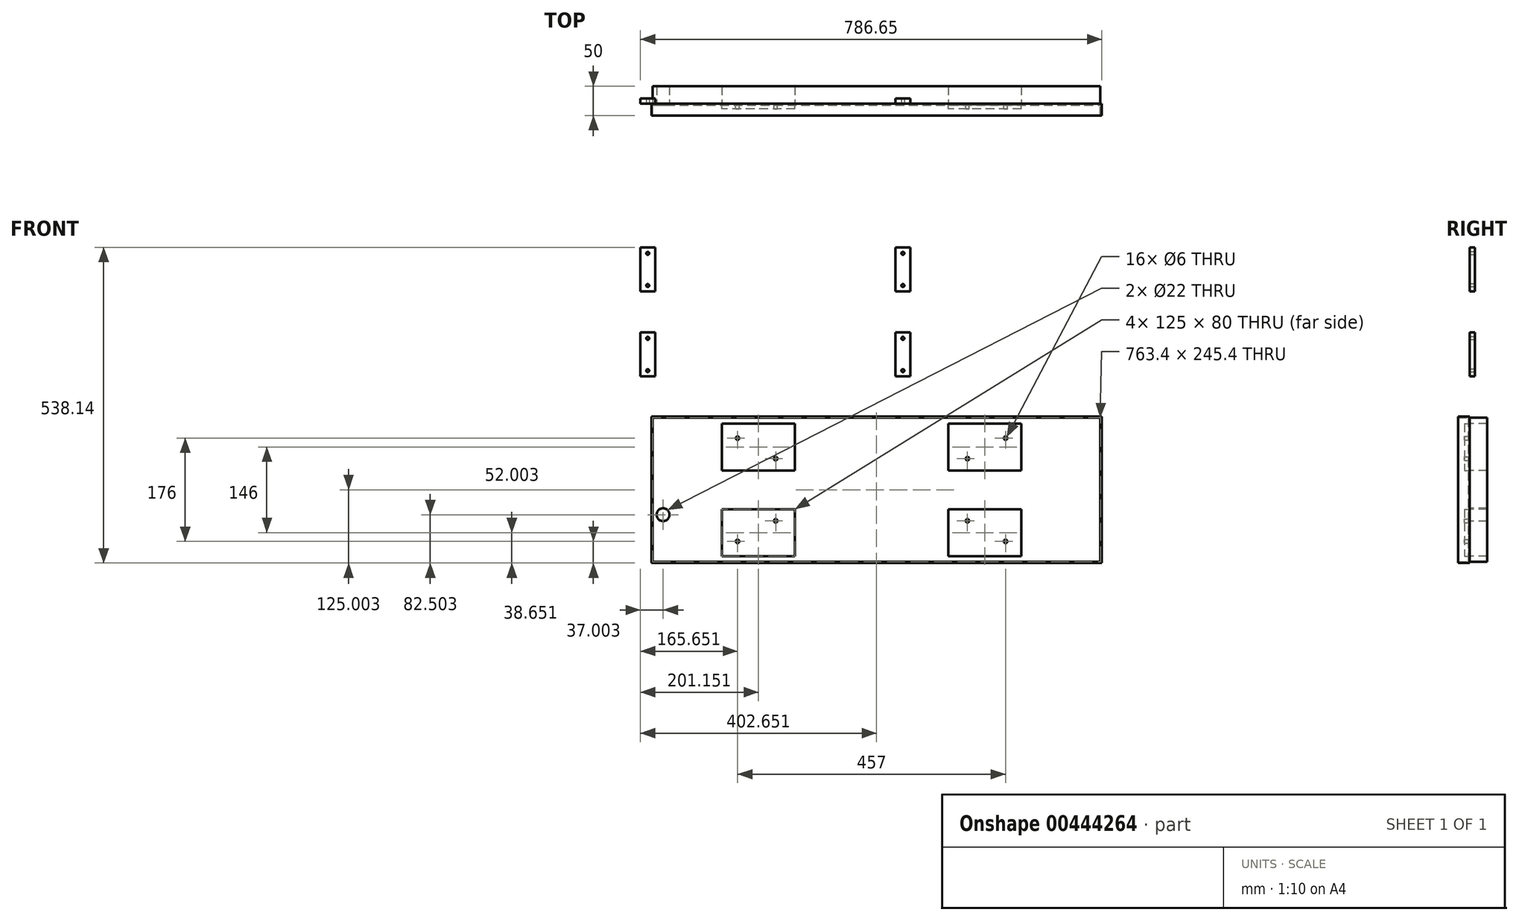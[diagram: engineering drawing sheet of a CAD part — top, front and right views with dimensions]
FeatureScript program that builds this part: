
annotation { "Feature Type Name" : "Feature", "Feature Type Description" : "" }
export const myFeature = defineFeature(function(context is Context, id is Id, definition is map)
    precondition{}
    {
        {
            var Q0;
            Q0=qCreatedBy(makeId("Front.planeOp"),FACE);
            var sketch = newSketch(context, id + "F0", { "sketchPlane" : qUnion([Q0])});
            skLineSegment(sketch, "E0", {"start": v(-733.37, -560) * mm, "end": v(-733.37, 560) * mm});
            skLineSegment(sketch, "E1", {"start": v(-733.37, -560) * mm, "end": v(876.63, -560) * mm});
            skLineSegment(sketch, "E2", {"start": v(-733.37, 560) * mm, "end": v(876.63, 560) * mm});
            skLineSegment(sketch, "E3", {"start": v(876.63, -560) * mm, "end": v(876.63, 560) * mm});
            skLineSegment(sketch, "E4", {"start": v(336.63, -506) * mm, "end": v(336.63, -560) * mm});
            skLineSegment(sketch, "E5", {"start": v(336.63, -506) * mm, "end": v(876.63, -506) * mm});
            skLineSegment(sketch, "E6", {"start": v(526.63, -552) * mm, "end": v(640.63, -552) * mm});
            skLineSegment(sketch, "E7", {"start": v(526.63, -533.38) * mm, "end": v(640.63, -533.38) * mm});
            skLineSegment(sketch, "E8", {"start": v(336.63, -544) * mm, "end": v(526.63, -544) * mm});
            skLineSegment(sketch, "E9", {"start": v(526.63, -506) * mm, "end": v(526.63, -560) * mm});
            skLineSegment(sketch, "E10", {"start": v(604.63, -533.38) * mm, "end": v(604.63, -560) * mm});
            skLineSegment(sketch, "E11", {"start": v(640.63, -542) * mm, "end": v(876.63, -542) * mm});
            skLineSegment(sketch, "E12", {"start": v(730.63, -524) * mm, "end": v(876.63, -524) * mm});
            skLineSegment(sketch, "E13", {"start": v(640.63, -516) * mm, "end": v(730.63, -516) * mm});
            skLineSegment(sketch, "E14", {"start": v(726.24, -520.82) * mm, "end": v(711.38, -538.9) * mm});
            skLineSegment(sketch, "E15", {"start": v(640.63, -506) * mm, "end": v(640.63, -560) * mm});
            skLineSegment(sketch, "E16", {"start": v(674.63, -506) * mm, "end": v(674.63, -542) * mm});
            skLineSegment(sketch, "E17", {"start": v(642.51, -529.04) * mm, "end": v(657.96, -529.04) * mm});
            skCircle(sketch, "E18", {"center": v(650.23, -529.04) * mm, "radius": 5.94 * mm});
            skCircle(sketch, "E19", {"center": v(650.23, -529.04) * mm, "radius": 2.93 * mm});
            skLineSegment(sketch, "E20", {"start": v(650.23, -521.32) * mm, "end": v(650.23, -536.77) * mm});
            skLineSegment(sketch, "E21", {"start": v(670.15, -523.1) * mm, "end": v(670.15, -534.99) * mm});
            skLineSegment(sketch, "E22", {"start": v(661.98, -526.11) * mm, "end": v(661.98, -531.98) * mm});
            skLineSegment(sketch, "E23", {"start": v(670.15, -534.99) * mm, "end": v(661.98, -531.98) * mm});
            skLineSegment(sketch, "E24", {"start": v(660.33, -529.04) * mm, "end": v(672, -529.04) * mm});
            skLineSegment(sketch, "E25", {"start": v(670.15, -523.1) * mm, "end": v(661.98, -526.11) * mm});
            skLineSegment(sketch, "E26", {"start": v(708.63, -506) * mm, "end": v(708.63, -542) * mm});
            skLineSegment(sketch, "E27", {"start": v(730.63, -506) * mm, "end": v(730.63, -542) * mm});
            skLineSegment(sketch, "E28", {"start": v(820.63, -542) * mm, "end": v(820.63, -560) * mm});
            skLineSegment(sketch, "E29", {"start": v(820.63, -506) * mm, "end": v(820.63, -524) * mm});
            skLineSegment(sketch, "E30", {"start": v(876.63, 548) * mm, "end": v(680.63, 548) * mm});
            skLineSegment(sketch, "E31", {"start": v(876.63, 536) * mm, "end": v(680.63, 536) * mm});
            skLineSegment(sketch, "E32", {"start": v(876.63, 524) * mm, "end": v(680.63, 524) * mm});
            skLineSegment(sketch, "E33", {"start": v(708.63, 560) * mm, "end": v(708.63, 524) * mm});
            skLineSegment(sketch, "E34", {"start": v(680.63, 560) * mm, "end": v(680.63, 524) * mm});
            skLineSegment(sketch, "E35", {"start": v(689.47, 550.2) * mm, "end": v(699.07, 550.2) * mm});
            skLineSegment(sketch, "E36", {"start": v(826.63, 560) * mm, "end": v(826.63, 524) * mm});
            skLineSegment(sketch, "E37", {"start": v(856.63, 560) * mm, "end": v(856.63, 524) * mm});
            skLineSegment(sketch, "E38", {"start": v(689.47, 550.2) * mm, "end": v(694.27, 558.2) * mm});
            skLineSegment(sketch, "E39", {"start": v(694.27, 558.2) * mm, "end": v(699.07, 550.2) * mm});
            skLineSegment(sketch, "E40", {"start": v(689.47, 538.2) * mm, "end": v(699.07, 538.2) * mm});
            skLineSegment(sketch, "E41", {"start": v(689.47, 538.2) * mm, "end": v(694.27, 546.2) * mm});
            skLineSegment(sketch, "E42", {"start": v(694.27, 546.2) * mm, "end": v(699.07, 538.2) * mm});
            skLineSegment(sketch, "E43", {"start": v(1010.4, -269.61) * mm, "end": v(1030.4, -269.61) * mm});
            skLineSegment(sketch, "E44", {"start": v(1030.4, -269.61) * mm, "end": v(1030.4, -249.61) * mm});
            skLineSegment(sketch, "E45", {"start": v(1030.4, -249.61) * mm, "end": v(1010.4, -269.61) * mm});
            skLineSegment(sketch, "E46", {"start": v(1013.65, 191.18) * mm, "end": v(1016.53, 186.18) * mm});
            skLineSegment(sketch, "E47", {"start": v(1016.53, 186.18) * mm, "end": v(1022.88, 197.18) * mm});
            skLineSegment(sketch, "E48", {"start": v(1022.88, 197.18) * mm, "end": v(1035.58, 197.18) * mm});
            skLineSegment(sketch, "E49", {"start": v(1013.65, 191.18) * mm, "end": v(1019.42, 191.18) * mm});
            skLineSegment(sketch, "E50", {"start": v(1039.7, 191.18) * mm, "end": v(1042.58, 186.18) * mm});
            skLineSegment(sketch, "E51", {"start": v(1042.58, 186.18) * mm, "end": v(1048.93, 197.18) * mm});
            skCircle(sketch, "E52", {"center": v(1042.58, 189.5) * mm, "radius": 1.67 * mm});
            skArc(sketch, "E53", {"start": v(1013.3, 197.53) * mm, "mid": v(1011.2, 191.68) * mm, "end": v(1013.3, 185.83) * mm});
            skArc(sketch, "E54", {"start": v(1053, 185.83) * mm, "mid": v(1055.1, 191.68) * mm, "end": v(1053, 197.53) * mm});
            skLineSegment(sketch, "E55", {"start": v(1036.28, 210.45) * mm, "end": v(1039.16, 205.45) * mm});
            skLineSegment(sketch, "E56", {"start": v(1039.16, 205.45) * mm, "end": v(1045.51, 216.45) * mm});
            skLineSegment(sketch, "E57", {"start": v(1045.51, 216.45) * mm, "end": v(1059.96, 216.45) * mm});
            skLineSegment(sketch, "E58", {"start": v(1036.28, 210.45) * mm, "end": v(1042.05, 210.45) * mm});
            skCircle(sketch, "E59", {"center": v(1045.51, 216.45) * mm, "radius": 1.57 * mm});
            skLineSegment(sketch, "E60", {"start": v(1032.26, 205.45) * mm, "end": v(1062.26, 205.45) * mm});
            skLineSegment(sketch, "E61", {"start": v(996.15, 134.22) * mm, "end": v(999.04, 129.22) * mm});
            skLineSegment(sketch, "E62", {"start": v(999.04, 129.22) * mm, "end": v(1005.4, 140.22) * mm});
            skLineSegment(sketch, "E63", {"start": v(1005.4, 140.22) * mm, "end": v(1019.84, 140.22) * mm});
            skLineSegment(sketch, "E64", {"start": v(996.15, 134.22) * mm, "end": v(1001.93, 134.22) * mm});
            skLineSegment(sketch, "E65", {"start": v(996.15, 114.48) * mm, "end": v(999.04, 109.48) * mm});
            skLineSegment(sketch, "E66", {"start": v(999.04, 109.48) * mm, "end": v(1005.4, 120.48) * mm});
            skLineSegment(sketch, "E67", {"start": v(1005.4, 120.48) * mm, "end": v(1019.84, 120.48) * mm});
            skLineSegment(sketch, "E68", {"start": v(996.15, 114.48) * mm, "end": v(1001.93, 114.48) * mm});
            skLineSegment(sketch, "E69", {"start": v(995.98, 95.05) * mm, "end": v(998.86, 90.05) * mm});
            skLineSegment(sketch, "E70", {"start": v(998.86, 90.05) * mm, "end": v(1005.21, 101.05) * mm});
            skLineSegment(sketch, "E71", {"start": v(1005.21, 101.05) * mm, "end": v(1017.9, 101.05) * mm});
            skLineSegment(sketch, "E72", {"start": v(995.98, 95.05) * mm, "end": v(1001.75, 95.05) * mm});
            skLineSegment(sketch, "E73", {"start": v(996.27, 77.08) * mm, "end": v(999.16, 72.08) * mm});
            skLineSegment(sketch, "E74", {"start": v(999.16, 72.08) * mm, "end": v(1005.51, 83.08) * mm});
            skLineSegment(sketch, "E75", {"start": v(1005.51, 83.08) * mm, "end": v(1018.27, 83.08) * mm});
            skLineSegment(sketch, "E76", {"start": v(996.27, 77.08) * mm, "end": v(1002.05, 77.08) * mm});
            skLineSegment(sketch, "E77", {"start": v(996.27, 59.66) * mm, "end": v(999.16, 54.66) * mm});
            skLineSegment(sketch, "E78", {"start": v(999.16, 54.66) * mm, "end": v(1005.51, 65.66) * mm});
            skLineSegment(sketch, "E79", {"start": v(1005.51, 65.66) * mm, "end": v(1018.27, 65.66) * mm});
            skLineSegment(sketch, "E80", {"start": v(996.27, 59.66) * mm, "end": v(1002.05, 59.66) * mm});
            skLineSegment(sketch, "E81", {"start": v(998.2, 306.77) * mm, "end": v(1001.09, 301.77) * mm});
            skLineSegment(sketch, "E82", {"start": v(1001.09, 301.77) * mm, "end": v(1007.44, 312.77) * mm});
            skLineSegment(sketch, "E83", {"start": v(1007.44, 312.77) * mm, "end": v(1021.88, 312.77) * mm});
            skLineSegment(sketch, "E84", {"start": v(998.2, 306.77) * mm, "end": v(1003.97, 306.77) * mm});
            skLineSegment(sketch, "E85", {"start": v(994.19, 301.77) * mm, "end": v(1024.19, 301.77) * mm});
            skLineSegment(sketch, "E86", {"start": v(998.2, 287.03) * mm, "end": v(1001.09, 282.03) * mm});
            skLineSegment(sketch, "E87", {"start": v(1001.09, 282.03) * mm, "end": v(1007.44, 293.03) * mm});
            skLineSegment(sketch, "E88", {"start": v(1007.44, 293.03) * mm, "end": v(1021.88, 293.03) * mm});
            skLineSegment(sketch, "E89", {"start": v(998.2, 287.03) * mm, "end": v(1003.97, 287.03) * mm});
            skLineSegment(sketch, "E90", {"start": v(994.19, 282.03) * mm, "end": v(1024.19, 282.03) * mm});
            skLineSegment(sketch, "E91", {"start": v(998.02, 267.6) * mm, "end": v(1000.9, 262.6) * mm});
            skLineSegment(sketch, "E92", {"start": v(1000.9, 262.6) * mm, "end": v(1007.26, 273.6) * mm});
            skLineSegment(sketch, "E93", {"start": v(1007.26, 273.6) * mm, "end": v(1019.95, 273.6) * mm});
            skLineSegment(sketch, "E94", {"start": v(998.02, 267.6) * mm, "end": v(1003.8, 267.6) * mm});
            skLineSegment(sketch, "E95", {"start": v(994, 262.6) * mm, "end": v(1024, 262.6) * mm});
            skLineSegment(sketch, "E96", {"start": v(998.32, 249.64) * mm, "end": v(1001.2, 244.64) * mm});
            skLineSegment(sketch, "E97", {"start": v(1001.2, 244.64) * mm, "end": v(1007.56, 255.64) * mm});
            skLineSegment(sketch, "E98", {"start": v(1007.56, 255.64) * mm, "end": v(1020.32, 255.64) * mm});
            skLineSegment(sketch, "E99", {"start": v(998.32, 249.64) * mm, "end": v(1004.1, 249.64) * mm});
            skLineSegment(sketch, "E100", {"start": v(994.3, 244.64) * mm, "end": v(1024.3, 244.64) * mm});
            skLineSegment(sketch, "E101", {"start": v(998.32, 232.21) * mm, "end": v(1001.2, 227.21) * mm});
            skLineSegment(sketch, "E102", {"start": v(1001.2, 227.21) * mm, "end": v(1007.56, 238.21) * mm});
            skLineSegment(sketch, "E103", {"start": v(1007.56, 238.21) * mm, "end": v(1020.32, 238.21) * mm});
            skLineSegment(sketch, "E104", {"start": v(998.32, 232.21) * mm, "end": v(1004.1, 232.21) * mm});
            skLineSegment(sketch, "E105", {"start": v(994.19, 227.42) * mm, "end": v(1024.19, 227.42) * mm});
            skLineSegment(sketch, "E106", {"start": v(998.72, 191.18) * mm, "end": v(1001.6, 186.18) * mm});
            skLineSegment(sketch, "E107", {"start": v(1001.6, 186.18) * mm, "end": v(1007.96, 197.18) * mm});
            skLineSegment(sketch, "E108", {"start": v(999.54, 210.87) * mm, "end": v(1002.43, 205.87) * mm});
            skLineSegment(sketch, "E109", {"start": v(1002.43, 205.87) * mm, "end": v(1008.78, 216.87) * mm});
            skCircle(sketch, "E110", {"center": v(1002.43, 209.2) * mm, "radius": 0.83 * mm});
            skLineSegment(sketch, "E111", {"start": v(996.43, 205.87) * mm, "end": v(1010.43, 205.87) * mm});
            skLineSegment(sketch, "E112", {"start": v(1018.14, 210.45) * mm, "end": v(1021.03, 205.45) * mm});
            skLineSegment(sketch, "E113", {"start": v(1021.03, 205.45) * mm, "end": v(1027.38, 216.45) * mm});
            skLineSegment(sketch, "E114", {"start": v(1018.14, 210.45) * mm, "end": v(1023.91, 210.45) * mm});
            skLineSegment(sketch, "E115", {"start": v(1015.03, 205.45) * mm, "end": v(1029.03, 205.45) * mm});
            skLineSegment(sketch, "E116", {"start": v(997.04, 174.08) * mm, "end": v(999.93, 169.08) * mm});
            skLineSegment(sketch, "E117", {"start": v(999.93, 169.08) * mm, "end": v(1006.28, 180.08) * mm});
            skLineSegment(sketch, "E118", {"start": v(1007.93, 169.08) * mm, "end": v(993.93, 169.08) * mm});
            skLineSegment(sketch, "E119", {"start": v(1040.3, 232.21) * mm, "end": v(1043.18, 227.21) * mm});
            skLineSegment(sketch, "E120", {"start": v(1043.18, 227.21) * mm, "end": v(1049.53, 238.21) * mm});
            skLineSegment(sketch, "E121", {"start": v(1049.53, 238.21) * mm, "end": v(1062.29, 238.21) * mm});
            skLineSegment(sketch, "E122", {"start": v(1040.3, 232.21) * mm, "end": v(1046.06, 232.21) * mm});
            skLineSegment(sketch, "E123", {"start": v(1036.16, 227.42) * mm, "end": v(1066.16, 227.42) * mm});
            skLineSegment(sketch, "E124", {"start": v(1040.3, 57.02) * mm, "end": v(1043.18, 52.02) * mm});
            skLineSegment(sketch, "E125", {"start": v(1043.18, 52.02) * mm, "end": v(1049.53, 63.02) * mm});
            skLineSegment(sketch, "E126", {"start": v(1049.53, 63.02) * mm, "end": v(1062.29, 63.02) * mm});
            skLineSegment(sketch, "E127", {"start": v(1040.3, 57.02) * mm, "end": v(1046.06, 57.02) * mm});
            skLineSegment(sketch, "E128", {"start": v(1016.1, 37.9) * mm, "end": v(1018.98, 32.9) * mm});
            skLineSegment(sketch, "E129", {"start": v(1018.98, 32.9) * mm, "end": v(1025.33, 43.9) * mm});
            skLineSegment(sketch, "E130", {"start": v(1016.1, 37.9) * mm, "end": v(1021.87, 37.9) * mm});
            skLineSegment(sketch, "E131", {"start": v(997.5, 38.32) * mm, "end": v(1000.38, 33.32) * mm});
            skLineSegment(sketch, "E132", {"start": v(1000.38, 33.32) * mm, "end": v(1006.73, 44.32) * mm});
            skCircle(sketch, "E133", {"center": v(1000.38, 36.65) * mm, "radius": 0.83 * mm});
            skLineSegment(sketch, "E134", {"start": v(517.21, 1.91) * mm, "end": v(-241.59, 1.91) * mm});
            skArc(sketch, "E135", {"start": v(517.21, 1.91) * mm, "mid": v(520.46, 3.26) * mm, "end": v(521.81, 6.51) * mm});
            skLineSegment(sketch, "E136", {"start": v(521.81, 21.91) * mm, "end": v(519.51, 21.91) * mm});
            skLineSegment(sketch, "E137", {"start": v(521.81, 6.51) * mm, "end": v(521.81, 21.91) * mm});
            skLineSegment(sketch, "E138", {"start": v(519.51, 6.51) * mm, "end": v(519.51, 21.91) * mm});
            skArc(sketch, "E139", {"start": v(517.21, 4.21) * mm, "mid": v(518.84, 4.89) * mm, "end": v(519.51, 6.51) * mm});
            skLineSegment(sketch, "E140", {"start": v(-246.19, 21.91) * mm, "end": v(-243.89, 21.91) * mm});
            skLineSegment(sketch, "E141", {"start": v(-246.19, 6.51) * mm, "end": v(-246.19, 21.91) * mm});
            skLineSegment(sketch, "E142", {"start": v(-243.89, 6.51) * mm, "end": v(-243.89, 21.91) * mm});
            skArc(sketch, "E143", {"start": v(-246.19, 6.51) * mm, "mid": v(-244.84, 3.26) * mm, "end": v(-241.59, 1.91) * mm});
            skArc(sketch, "E144", {"start": v(-243.89, 6.51) * mm, "mid": v(-243.22, 4.89) * mm, "end": v(-241.59, 4.21) * mm});
            skLineSegment(sketch, "E145", {"start": v(517.21, 4.21) * mm, "end": v(-241.59, 4.21) * mm});
            skLineSegment(sketch, "E146", {"start": v(384.81, 13.21) * mm, "end": v(259.81, 13.21) * mm});
            skLineSegment(sketch, "E147", {"start": v(-246.19, 21.91) * mm, "end": v(521.81, 21.91) * mm});
            skLineSegment(sketch, "E148", {"start": v(-62.19, -7.09) * mm, "end": v(-87.19, -7.09) * mm});
            skLineSegment(sketch, "E149", {"start": v(-87.19, 1.91) * mm, "end": v(-87.19, -7.09) * mm});
            skLineSegment(sketch, "E150", {"start": v(-62.19, 1.91) * mm, "end": v(-62.19, -7.09) * mm});
            skLineSegment(sketch, "E151", {"start": v(347.81, -7.09) * mm, "end": v(372.81, -7.09) * mm});
            skLineSegment(sketch, "E152", {"start": v(372.81, 1.91) * mm, "end": v(372.81, -7.09) * mm});
            skLineSegment(sketch, "E153", {"start": v(347.81, 1.91) * mm, "end": v(347.81, -7.09) * mm});
            skLineSegment(sketch, "E154", {"start": v(-387.97, 4.21) * mm, "end": v(-628.77, 4.21) * mm});
            skLineSegment(sketch, "E155", {"start": v(-387.97, 1.91) * mm, "end": v(-628.77, 1.91) * mm});
            skLineSegment(sketch, "E156", {"start": v(-398.37, -7.09) * mm, "end": v(-454.87, -7.09) * mm});
            skArc(sketch, "E157", {"start": v(-387.97, 1.91) * mm, "mid": v(-384.72, 3.26) * mm, "end": v(-383.37, 6.51) * mm});
            skLineSegment(sketch, "E158", {"start": v(-383.37, 21.91) * mm, "end": v(-385.67, 21.91) * mm});
            skLineSegment(sketch, "E159", {"start": v(-383.37, 6.51) * mm, "end": v(-383.37, 21.91) * mm});
            skLineSegment(sketch, "E160", {"start": v(-385.67, 6.51) * mm, "end": v(-385.67, 21.91) * mm});
            skArc(sketch, "E161", {"start": v(-387.97, 4.21) * mm, "mid": v(-386.34, 4.89) * mm, "end": v(-385.67, 6.51) * mm});
            skLineSegment(sketch, "E162", {"start": v(-633.37, 6.51) * mm, "end": v(-633.37, 21.91) * mm});
            skLineSegment(sketch, "E163", {"start": v(-631.07, 6.51) * mm, "end": v(-631.07, 21.91) * mm});
            skArc(sketch, "E164", {"start": v(-633.37, 6.51) * mm, "mid": v(-632.02, 3.26) * mm, "end": v(-628.77, 1.91) * mm});
            skArc(sketch, "E165", {"start": v(-631.07, 6.51) * mm, "mid": v(-630.4, 4.89) * mm, "end": v(-628.77, 4.21) * mm});
            skLineSegment(sketch, "E166", {"start": v(-398.37, 1.91) * mm, "end": v(-398.37, -7.09) * mm});
            skLineSegment(sketch, "E167", {"start": v(-473.37, 1.91) * mm, "end": v(-473.37, -7.09) * mm});
            skLineSegment(sketch, "E168", {"start": v(-618.37, -7.09) * mm, "end": v(-543.37, -7.09) * mm});
            skLineSegment(sketch, "E169", {"start": v(-618.37, 1.91) * mm, "end": v(-618.37, -7.09) * mm});
            skLineSegment(sketch, "E170", {"start": v(-543.37, 1.91) * mm, "end": v(-543.37, -7.09) * mm});
            skLineSegment(sketch, "E171", {"start": v(-383.37, 21.91) * mm, "end": v(-633.37, 21.91) * mm});
            skLineSegment(sketch, "E172", {"start": v(-233.44, -8.09) * mm, "end": v(-233.75, 1.91) * mm});
            skLineSegment(sketch, "E173", {"start": v(-234.02, -18.09) * mm, "end": v(-218.36, -18.09) * mm});
            skLineSegment(sketch, "E174", {"start": v(-226.19, 1.91) * mm, "end": v(-226.19, -16.4) * mm});
            skLineSegment(sketch, "E175", {"start": v(-235.19, 4.21) * mm, "end": v(-235.19, 1.91) * mm});
            skLineSegment(sketch, "E176", {"start": v(-233.44, -18.09) * mm, "end": v(-233.44, -14.8) * mm});
            skLineSegment(sketch, "E177", {"start": v(-233.44, -8.09) * mm, "end": v(-233.44, -14.8) * mm});
            skLineSegment(sketch, "E178", {"start": v(-234.02, -18.09) * mm, "end": v(-234.52, -28.09) * mm});
            skLineSegment(sketch, "E179", {"start": v(-234.02, -8.09) * mm, "end": v(-218.36, -8.09) * mm});
            skLineSegment(sketch, "E180", {"start": v(-234.02, -8.09) * mm, "end": v(-233.44, -9.1) * mm});
            skLineSegment(sketch, "E181", {"start": v(-218.94, -18.09) * mm, "end": v(-218.94, -14.8) * mm});
            skLineSegment(sketch, "E182", {"start": v(-234.02, -18.09) * mm, "end": v(-233.44, -17.08) * mm});
            skLineSegment(sketch, "E183", {"start": v(-215.19, -28.09) * mm, "end": v(-237.19, -28.09) * mm});
            skLineSegment(sketch, "E184", {"start": v(-218.94, -8.09) * mm, "end": v(-218.94, -14.8) * mm});
            skLineSegment(sketch, "E185", {"start": v(-215.19, 1.91) * mm, "end": v(-237.19, 1.91) * mm});
            skLineSegment(sketch, "E186", {"start": v(-226.19, -28.09) * mm, "end": v(-226.19, -9.76) * mm});
            skLineSegment(sketch, "E187", {"start": v(-215.19, 1.91) * mm, "end": v(-215.19, -28.09) * mm});
            skLineSegment(sketch, "E188", {"start": v(-233.44, -18.09) * mm, "end": v(-233.75, -28.09) * mm});
            skLineSegment(sketch, "E189", {"start": v(-234.02, -8.09) * mm, "end": v(-234.52, 1.91) * mm});
            skLineSegment(sketch, "E190", {"start": v(-217.19, 4.21) * mm, "end": v(-217.19, 1.91) * mm});
            skLineSegment(sketch, "E191", {"start": v(-218.36, -8.09) * mm, "end": v(-218.94, -9.1) * mm});
            skLineSegment(sketch, "E192", {"start": v(-237.19, 1.91) * mm, "end": v(-237.19, -28.09) * mm});
            skLineSegment(sketch, "E193", {"start": v(-218.94, -18.09) * mm, "end": v(-218.63, -28.09) * mm});
            skLineSegment(sketch, "E194", {"start": v(-218.36, -18.09) * mm, "end": v(-218.94, -17.08) * mm});
            skLineSegment(sketch, "E195", {"start": v(-218.36, -8.09) * mm, "end": v(-217.86, 1.91) * mm});
            skLineSegment(sketch, "E196", {"start": v(-218.94, -8.09) * mm, "end": v(-218.63, 1.91) * mm});
            skLineSegment(sketch, "E197", {"start": v(-218.36, -18.09) * mm, "end": v(-217.86, -28.09) * mm});
            skLineSegment(sketch, "E198", {"start": v(521.81, 149.05) * mm, "end": v(521.81, 399.05) * mm});
            skLineSegment(sketch, "E199", {"start": v(519.51, 151.35) * mm, "end": v(519.51, 396.75) * mm});
            skLineSegment(sketch, "E200", {"start": v(-246.19, 149.05) * mm, "end": v(-246.19, 399.05) * mm});
            skLineSegment(sketch, "E201", {"start": v(-243.89, 151.35) * mm, "end": v(-243.89, 396.75) * mm});
            skLineSegment(sketch, "E202", {"start": v(-246.19, 149.05) * mm, "end": v(521.81, 149.05) * mm});
            skLineSegment(sketch, "E203", {"start": v(-243.89, 151.35) * mm, "end": v(519.51, 151.35) * mm});
            skLineSegment(sketch, "E204", {"start": v(-246.19, 399.05) * mm, "end": v(521.81, 399.05) * mm});
            skLineSegment(sketch, "E205", {"start": v(-243.89, 396.75) * mm, "end": v(519.51, 396.75) * mm});
            skLineSegment(sketch, "E206", {"start": v(384.81, 13.21) * mm, "end": v(384.81, 4.21) * mm});
            skLineSegment(sketch, "E207", {"start": v(259.81, 13.21) * mm, "end": v(259.81, 4.21) * mm});
            skLineSegment(sketch, "E208", {"start": v(-395.37, 13.21) * mm, "end": v(-395.37, 4.21) * mm});
            skLineSegment(sketch, "E209", {"start": v(-475.37, 13.21) * mm, "end": v(-475.37, 4.21) * mm});
            skLineSegment(sketch, "E210", {"start": v(-473.12, -8.09) * mm, "end": v(-473.43, 1.91) * mm});
            skLineSegment(sketch, "E211", {"start": v(-473.7, -18.09) * mm, "end": v(-458.04, -18.09) * mm});
            skLineSegment(sketch, "E212", {"start": v(-465.87, 1.91) * mm, "end": v(-465.87, -16.4) * mm});
            skLineSegment(sketch, "E213", {"start": v(-474.87, 4.21) * mm, "end": v(-474.87, 1.91) * mm});
            skLineSegment(sketch, "E214", {"start": v(-473.12, -18.09) * mm, "end": v(-473.12, -14.8) * mm});
            skLineSegment(sketch, "E215", {"start": v(-473.12, -8.09) * mm, "end": v(-473.12, -14.8) * mm});
            skLineSegment(sketch, "E216", {"start": v(-473.7, -18.09) * mm, "end": v(-474.2, -28.09) * mm});
            skLineSegment(sketch, "E217", {"start": v(-473.7, -8.09) * mm, "end": v(-458.04, -8.09) * mm});
            skLineSegment(sketch, "E218", {"start": v(-473.7, -8.09) * mm, "end": v(-473.12, -9.1) * mm});
            skLineSegment(sketch, "E219", {"start": v(-458.62, -18.09) * mm, "end": v(-458.62, -14.8) * mm});
            skLineSegment(sketch, "E220", {"start": v(-473.7, -18.09) * mm, "end": v(-473.12, -17.08) * mm});
            skLineSegment(sketch, "E221", {"start": v(-454.87, -28.09) * mm, "end": v(-476.87, -28.09) * mm});
            skLineSegment(sketch, "E222", {"start": v(-458.62, -8.09) * mm, "end": v(-458.62, -14.8) * mm});
            skLineSegment(sketch, "E223", {"start": v(-454.87, 1.91) * mm, "end": v(-476.87, 1.91) * mm});
            skLineSegment(sketch, "E224", {"start": v(-465.87, -28.09) * mm, "end": v(-465.87, -9.76) * mm});
            skLineSegment(sketch, "E225", {"start": v(-454.87, 1.91) * mm, "end": v(-454.87, -28.09) * mm});
            skLineSegment(sketch, "E226", {"start": v(-473.12, -18.09) * mm, "end": v(-473.43, -28.09) * mm});
            skLineSegment(sketch, "E227", {"start": v(-473.7, -8.09) * mm, "end": v(-474.2, 1.91) * mm});
            skLineSegment(sketch, "E228", {"start": v(-456.87, 4.21) * mm, "end": v(-456.87, 1.91) * mm});
            skLineSegment(sketch, "E229", {"start": v(-458.04, -8.09) * mm, "end": v(-458.62, -9.1) * mm});
            skLineSegment(sketch, "E230", {"start": v(-476.87, 1.91) * mm, "end": v(-476.87, -28.09) * mm});
            skLineSegment(sketch, "E231", {"start": v(-458.62, -18.09) * mm, "end": v(-458.3, -28.09) * mm});
            skLineSegment(sketch, "E232", {"start": v(-458.04, -18.09) * mm, "end": v(-458.62, -17.08) * mm});
            skLineSegment(sketch, "E233", {"start": v(-458.04, -8.09) * mm, "end": v(-457.54, 1.91) * mm});
            skLineSegment(sketch, "E234", {"start": v(-458.62, -8.09) * mm, "end": v(-458.3, 1.91) * mm});
            skLineSegment(sketch, "E235", {"start": v(-458.04, -18.09) * mm, "end": v(-457.54, -28.09) * mm});
            skLineSegment(sketch, "E236", {"start": v(-126.19, 13.21) * mm, "end": v(-1.19, 13.21) * mm});
            skLineSegment(sketch, "E237", {"start": v(-126.19, 13.21) * mm, "end": v(-126.19, 4.21) * mm});
            skLineSegment(sketch, "E238", {"start": v(-1.19, 13.21) * mm, "end": v(-1.19, 4.21) * mm});
            skLineSegment(sketch, "E239", {"start": v(-475.37, 13.21) * mm, "end": v(-395.37, 13.21) * mm});
            skLineSegment(sketch, "E240", {"start": v(-541.37, 13.21) * mm, "end": v(-541.37, 4.21) * mm});
            skLineSegment(sketch, "E241", {"start": v(-621.37, 13.21) * mm, "end": v(-621.37, 4.21) * mm});
            skLineSegment(sketch, "E242", {"start": v(-621.37, 13.21) * mm, "end": v(-541.37, 13.21) * mm});
            skCircle(sketch, "E243", {"center": v(-226.19, 231.55) * mm, "radius": 11 * mm});
            skLineSegment(sketch, "E244", {"start": v(-1.19, 387.05) * mm, "end": v(-1.19, 307.05) * mm});
            skLineSegment(sketch, "E245", {"start": v(-1.19, 241.05) * mm, "end": v(-1.19, 161.05) * mm});
            skLineSegment(sketch, "E246", {"start": v(-126.19, 387.05) * mm, "end": v(-126.19, 307.05) * mm});
            skLineSegment(sketch, "E247", {"start": v(-126.19, 241.05) * mm, "end": v(-126.19, 161.05) * mm});
            skLineSegment(sketch, "E248", {"start": v(259.81, 387.05) * mm, "end": v(259.81, 307.05) * mm});
            skLineSegment(sketch, "E249", {"start": v(259.81, 241.05) * mm, "end": v(259.81, 161.05) * mm});
            skLineSegment(sketch, "E250", {"start": v(384.81, 387.05) * mm, "end": v(384.81, 307.05) * mm});
            skLineSegment(sketch, "E251", {"start": v(384.81, 241.05) * mm, "end": v(384.81, 161.05) * mm});
            skLineSegment(sketch, "E252", {"start": v(384.81, 307.05) * mm, "end": v(259.81, 307.05) * mm});
            skLineSegment(sketch, "E253", {"start": v(-1.19, 307.05) * mm, "end": v(-126.19, 307.05) * mm});
            skLineSegment(sketch, "E254", {"start": v(384.81, 387.05) * mm, "end": v(259.81, 387.05) * mm});
            skLineSegment(sketch, "E255", {"start": v(-1.19, 387.05) * mm, "end": v(-126.19, 387.05) * mm});
            skLineSegment(sketch, "E256", {"start": v(384.81, 161.05) * mm, "end": v(259.81, 161.05) * mm});
            skLineSegment(sketch, "E257", {"start": v(-1.19, 161.05) * mm, "end": v(-126.19, 161.05) * mm});
            skLineSegment(sketch, "E258", {"start": v(384.81, 241.05) * mm, "end": v(259.81, 241.05) * mm});
            skLineSegment(sketch, "E259", {"start": v(-1.19, 241.05) * mm, "end": v(-126.19, 241.05) * mm});
            skLineSegment(sketch, "E260", {"start": v(362.31, 186.05) * mm, "end": v(353.31, 186.05) * mm});
            skCircle(sketch, "E261", {"center": v(357.81, 186.05) * mm, "radius": 3 * mm});
            skLineSegment(sketch, "E262", {"start": v(357.81, 181.55) * mm, "end": v(357.81, 190.55) * mm});
            skCircle(sketch, "E263", {"center": v(357.81, 186.05) * mm, "radius": 2.46 * mm});
            skLineSegment(sketch, "E264", {"start": v(-94.69, 186.05) * mm, "end": v(-103.69, 186.05) * mm});
            skCircle(sketch, "E265", {"center": v(-99.19, 186.05) * mm, "radius": 3 * mm});
            skLineSegment(sketch, "E266", {"start": v(-99.19, 181.55) * mm, "end": v(-99.19, 190.55) * mm});
            skCircle(sketch, "E267", {"center": v(-99.19, 186.05) * mm, "radius": 2.46 * mm});
            skLineSegment(sketch, "E268", {"start": v(297.31, 221.05) * mm, "end": v(288.31, 221.05) * mm});
            skCircle(sketch, "E269", {"center": v(292.81, 221.05) * mm, "radius": 3 * mm});
            skLineSegment(sketch, "E270", {"start": v(292.81, 216.55) * mm, "end": v(292.81, 225.55) * mm});
            skCircle(sketch, "E271", {"center": v(292.81, 221.05) * mm, "radius": 2.46 * mm});
            skLineSegment(sketch, "E272", {"start": v(-29.69, 221.05) * mm, "end": v(-38.69, 221.05) * mm});
            skCircle(sketch, "E273", {"center": v(-34.19, 221.05) * mm, "radius": 3 * mm});
            skLineSegment(sketch, "E274", {"start": v(-34.19, 216.55) * mm, "end": v(-34.19, 225.55) * mm});
            skCircle(sketch, "E275", {"center": v(-34.19, 221.05) * mm, "radius": 2.46 * mm});
            skLineSegment(sketch, "E276", {"start": v(362.31, 362.05) * mm, "end": v(353.31, 362.05) * mm});
            skCircle(sketch, "E277", {"center": v(357.81, 362.05) * mm, "radius": 3 * mm});
            skLineSegment(sketch, "E278", {"start": v(357.81, 366.55) * mm, "end": v(357.81, 357.55) * mm});
            skCircle(sketch, "E279", {"center": v(357.81, 362.05) * mm, "radius": 2.46 * mm});
            skLineSegment(sketch, "E280", {"start": v(-94.69, 362.05) * mm, "end": v(-103.69, 362.05) * mm});
            skCircle(sketch, "E281", {"center": v(-99.19, 362.05) * mm, "radius": 3 * mm});
            skLineSegment(sketch, "E282", {"start": v(-99.19, 366.55) * mm, "end": v(-99.19, 357.55) * mm});
            skCircle(sketch, "E283", {"center": v(-99.19, 362.05) * mm, "radius": 2.46 * mm});
            skLineSegment(sketch, "E284", {"start": v(297.31, 327.05) * mm, "end": v(288.31, 327.05) * mm});
            skCircle(sketch, "E285", {"center": v(292.81, 327.05) * mm, "radius": 3 * mm});
            skLineSegment(sketch, "E286", {"start": v(292.81, 331.55) * mm, "end": v(292.81, 322.55) * mm});
            skCircle(sketch, "E287", {"center": v(292.81, 327.05) * mm, "radius": 2.46 * mm});
            skLineSegment(sketch, "E288", {"start": v(-29.69, 327.05) * mm, "end": v(-38.69, 327.05) * mm});
            skCircle(sketch, "E289", {"center": v(-34.19, 327.05) * mm, "radius": 3 * mm});
            skLineSegment(sketch, "E290", {"start": v(-34.19, 331.55) * mm, "end": v(-34.19, 322.55) * mm});
            skCircle(sketch, "E291", {"center": v(-34.19, 327.05) * mm, "radius": 2.46 * mm});
            skLineSegment(sketch, "E292", {"start": v(521.81, -164.08) * mm, "end": v(521.81, -414.08) * mm});
            skLineSegment(sketch, "E293", {"start": v(519.51, -166.38) * mm, "end": v(519.51, -411.78) * mm});
            skLineSegment(sketch, "E294", {"start": v(-246.19, -164.08) * mm, "end": v(-246.19, -414.08) * mm});
            skLineSegment(sketch, "E295", {"start": v(-243.89, -166.38) * mm, "end": v(-243.89, -411.78) * mm});
            skLineSegment(sketch, "E296", {"start": v(-246.19, -164.08) * mm, "end": v(521.81, -164.08) * mm});
            skLineSegment(sketch, "E297", {"start": v(-243.89, -166.38) * mm, "end": v(519.51, -166.38) * mm});
            skLineSegment(sketch, "E298", {"start": v(-246.19, -414.08) * mm, "end": v(521.81, -414.08) * mm});
            skLineSegment(sketch, "E299", {"start": v(-243.89, -411.78) * mm, "end": v(519.51, -411.78) * mm});
            skCircle(sketch, "E300", {"center": v(-226.19, -246.58) * mm, "radius": 7 * mm});
            skLineSegment(sketch, "E301", {"start": v(-217.09, -246.58) * mm, "end": v(-235.29, -246.58) * mm});
            skLineSegment(sketch, "E302", {"start": v(-226.19, -255.68) * mm, "end": v(-226.19, -237.48) * mm});
            skCircle(sketch, "E303", {"center": v(-226.19, -246.58) * mm, "radius": 11 * mm});
            skCircle(sketch, "E304", {"center": v(-226.19, -246.58) * mm, "radius": 7.56 * mm});
            skCircle(sketch, "E305", {"center": v(-226.19, -246.58) * mm, "radius": 8.33 * mm});
            skLineSegment(sketch, "E306", {"start": v(-62.19, -179.08) * mm, "end": v(-62.19, -254.08) * mm});
            skLineSegment(sketch, "E307", {"start": v(-62.19, -324.08) * mm, "end": v(-62.19, -399.08) * mm});
            skLineSegment(sketch, "E308", {"start": v(-91.04, -180) * mm, "end": v(-91.04, -255) * mm});
            skLineSegment(sketch, "E309", {"start": v(-87.19, -324.08) * mm, "end": v(-87.19, -399.08) * mm});
            skLineSegment(sketch, "E310", {"start": v(347.81, -179.08) * mm, "end": v(347.81, -254.08) * mm});
            skLineSegment(sketch, "E311", {"start": v(347.81, -324.08) * mm, "end": v(347.81, -399.08) * mm});
            skLineSegment(sketch, "E312", {"start": v(372.81, -179.08) * mm, "end": v(372.81, -254.08) * mm});
            skLineSegment(sketch, "E313", {"start": v(372.81, -324.08) * mm, "end": v(372.81, -399.08) * mm});
            skLineSegment(sketch, "E314", {"start": v(372.81, -179.08) * mm, "end": v(347.81, -179.08) * mm});
            skLineSegment(sketch, "E315", {"start": v(-66.04, -180) * mm, "end": v(-91.04, -180) * mm});
            skLineSegment(sketch, "E316", {"start": v(372.81, -254.08) * mm, "end": v(347.81, -254.08) * mm});
            skLineSegment(sketch, "E317", {"start": v(-66.04, -255) * mm, "end": v(-91.04, -255) * mm});
            skLineSegment(sketch, "E318", {"start": v(372.81, -324.08) * mm, "end": v(347.81, -324.08) * mm});
            skLineSegment(sketch, "E319", {"start": v(-62.19, -324.08) * mm, "end": v(-87.19, -324.08) * mm});
            skLineSegment(sketch, "E320", {"start": v(372.81, -399.08) * mm, "end": v(347.81, -399.08) * mm});
            skLineSegment(sketch, "E321", {"start": v(-62.19, -399.08) * mm, "end": v(-87.19, -399.08) * mm});
            skLineSegment(sketch, "E322", {"start": v(-74.69, -192.83) * mm, "end": v(-74.69, -185.33) * mm});
            skCircle(sketch, "E323", {"center": v(-74.69, -189.08) * mm, "radius": 2.07 * mm});
            skCircle(sketch, "E324", {"center": v(-74.69, -189.08) * mm, "radius": 2.5 * mm});
            skLineSegment(sketch, "E325", {"start": v(-70.94, -189.08) * mm, "end": v(-78.44, -189.08) * mm});
            skLineSegment(sketch, "E326", {"start": v(-74.69, -247.83) * mm, "end": v(-74.69, -240.33) * mm});
            skCircle(sketch, "E327", {"center": v(-74.69, -244.08) * mm, "radius": 2.07 * mm});
            skCircle(sketch, "E328", {"center": v(-74.69, -244.08) * mm, "radius": 2.5 * mm});
            skLineSegment(sketch, "E329", {"start": v(-70.94, -244.08) * mm, "end": v(-78.44, -244.08) * mm});
            skLineSegment(sketch, "E330", {"start": v(-74.69, -337.83) * mm, "end": v(-74.69, -330.33) * mm});
            skCircle(sketch, "E331", {"center": v(-74.69, -334.08) * mm, "radius": 2.07 * mm});
            skCircle(sketch, "E332", {"center": v(-74.69, -334.08) * mm, "radius": 2.5 * mm});
            skLineSegment(sketch, "E333", {"start": v(-70.94, -334.08) * mm, "end": v(-78.44, -334.08) * mm});
            skLineSegment(sketch, "E334", {"start": v(-74.69, -392.83) * mm, "end": v(-74.69, -385.33) * mm});
            skCircle(sketch, "E335", {"center": v(-74.69, -389.08) * mm, "radius": 2.07 * mm});
            skCircle(sketch, "E336", {"center": v(-74.69, -389.08) * mm, "radius": 2.5 * mm});
            skLineSegment(sketch, "E337", {"start": v(-70.94, -389.08) * mm, "end": v(-78.44, -389.08) * mm});
            skLineSegment(sketch, "E338", {"start": v(360.31, -337.83) * mm, "end": v(360.31, -330.33) * mm});
            skCircle(sketch, "E339", {"center": v(360.31, -334.08) * mm, "radius": 2.07 * mm});
            skCircle(sketch, "E340", {"center": v(360.31, -334.08) * mm, "radius": 2.5 * mm});
            skLineSegment(sketch, "E341", {"start": v(364.06, -334.08) * mm, "end": v(356.56, -334.08) * mm});
            skLineSegment(sketch, "E342", {"start": v(360.31, -392.83) * mm, "end": v(360.31, -385.33) * mm});
            skCircle(sketch, "E343", {"center": v(360.31, -389.08) * mm, "radius": 2.07 * mm});
            skCircle(sketch, "E344", {"center": v(360.31, -389.08) * mm, "radius": 2.5 * mm});
            skLineSegment(sketch, "E345", {"start": v(364.06, -389.08) * mm, "end": v(356.56, -389.08) * mm});
            skLineSegment(sketch, "E346", {"start": v(360.31, -192.83) * mm, "end": v(360.31, -185.33) * mm});
            skCircle(sketch, "E347", {"center": v(360.31, -189.08) * mm, "radius": 2.07 * mm});
            skCircle(sketch, "E348", {"center": v(360.31, -189.08) * mm, "radius": 2.5 * mm});
            skLineSegment(sketch, "E349", {"start": v(364.06, -189.08) * mm, "end": v(356.56, -189.08) * mm});
            skLineSegment(sketch, "E350", {"start": v(360.31, -247.83) * mm, "end": v(360.31, -240.33) * mm});
            skCircle(sketch, "E351", {"center": v(360.31, -244.08) * mm, "radius": 2.07 * mm});
            skCircle(sketch, "E352", {"center": v(360.31, -244.08) * mm, "radius": 2.5 * mm});
            skLineSegment(sketch, "E353", {"start": v(364.06, -244.08) * mm, "end": v(356.56, -244.08) * mm});
            skCircle(sketch, "E354", {"center": v(-226.19, 231.55) * mm, "radius": 9 * mm});
            skLineSegment(sketch, "E355", {"start": v(-214.49, 231.55) * mm, "end": v(-237.89, 231.55) * mm});
            skLineSegment(sketch, "E356", {"start": v(-226.19, 243.25) * mm, "end": v(-226.19, 219.85) * mm});
            skLineSegment(sketch, "E357", {"start": v(582.86, -523.17) * mm, "end": v(585.74, -528.17) * mm});
            skLineSegment(sketch, "E358", {"start": v(585.74, -528.17) * mm, "end": v(592.1, -517.17) * mm});
            skLineSegment(sketch, "E359", {"start": v(495.66, 500.85) * mm, "end": v(512.5, 500.85) * mm});
            skLineSegment(sketch, "E360", {"start": v(458.33, -451) * mm, "end": v(475.16, -451) * mm});
            skLineSegment(sketch, "E361", {"start": v(-454.87, -7.09) * mm, "end": v(-473.37, -7.09) * mm});
            skLineSegment(sketch, "E362", {"start": v(344.16, 952.19) * mm, "end": v(344.16, 702.19) * mm});
            skLineSegment(sketch, "E363", {"start": v(341.86, 949.89) * mm, "end": v(341.86, 704.49) * mm});
            skLineSegment(sketch, "E364", {"start": v(-423.84, 952.19) * mm, "end": v(-423.84, 702.19) * mm});
            skLineSegment(sketch, "E365", {"start": v(-421.54, 949.89) * mm, "end": v(-421.54, 704.49) * mm});
            skLineSegment(sketch, "E366", {"start": v(-423.84, 952.19) * mm, "end": v(344.16, 952.19) * mm});
            skLineSegment(sketch, "E367", {"start": v(-421.54, 949.89) * mm, "end": v(341.86, 949.89) * mm});
            skLineSegment(sketch, "E368", {"start": v(-423.84, 702.19) * mm, "end": v(344.16, 702.19) * mm});
            skLineSegment(sketch, "E369", {"start": v(-421.54, 704.49) * mm, "end": v(341.86, 704.49) * mm});
            skCircle(sketch, "E370", {"center": v(-403.84, 869.69) * mm, "radius": 7 * mm});
            skLineSegment(sketch, "E371", {"start": v(-394.74, 869.69) * mm, "end": v(-412.94, 869.69) * mm});
            skLineSegment(sketch, "E372", {"start": v(-403.84, 860.59) * mm, "end": v(-403.84, 878.79) * mm});
            skCircle(sketch, "E373", {"center": v(-403.84, 869.69) * mm, "radius": 11 * mm});
            skCircle(sketch, "E374", {"center": v(-403.84, 869.69) * mm, "radius": 7.56 * mm});
            skCircle(sketch, "E375", {"center": v(-403.84, 869.69) * mm, "radius": 8.33 * mm});
            skLineSegment(sketch, "E376", {"start": v(-239.84, 937.19) * mm, "end": v(-239.84, 862.19) * mm});
            skLineSegment(sketch, "E377", {"start": v(-239.84, 792.19) * mm, "end": v(-239.84, 717.19) * mm});
            skLineSegment(sketch, "E378", {"start": v(-264.84, 937.19) * mm, "end": v(-264.84, 862.19) * mm});
            skLineSegment(sketch, "E379", {"start": v(-264.84, 792.19) * mm, "end": v(-264.84, 717.19) * mm});
            skLineSegment(sketch, "E380", {"start": v(170.16, 937.19) * mm, "end": v(170.16, 862.19) * mm});
            skLineSegment(sketch, "E381", {"start": v(170.16, 792.19) * mm, "end": v(170.16, 717.19) * mm});
            skLineSegment(sketch, "E382", {"start": v(195.16, 937.19) * mm, "end": v(195.16, 862.19) * mm});
            skLineSegment(sketch, "E383", {"start": v(195.16, 792.19) * mm, "end": v(195.16, 717.19) * mm});
            skLineSegment(sketch, "E384", {"start": v(195.16, 937.19) * mm, "end": v(170.16, 937.19) * mm});
            skLineSegment(sketch, "E385", {"start": v(-239.84, 937.19) * mm, "end": v(-264.84, 937.19) * mm});
            skLineSegment(sketch, "E386", {"start": v(195.16, 862.19) * mm, "end": v(170.16, 862.19) * mm});
            skLineSegment(sketch, "E387", {"start": v(-239.84, 862.19) * mm, "end": v(-261, 862.19) * mm});
            skLineSegment(sketch, "E388", {"start": v(195.16, 792.19) * mm, "end": v(170.16, 792.19) * mm});
            skLineSegment(sketch, "E389", {"start": v(-239.84, 792.19) * mm, "end": v(-264.84, 792.19) * mm});
            skLineSegment(sketch, "E390", {"start": v(195.16, 717.19) * mm, "end": v(170.16, 717.19) * mm});
            skLineSegment(sketch, "E391", {"start": v(-239.84, 717.19) * mm, "end": v(-264.84, 717.19) * mm});
            skLineSegment(sketch, "E392", {"start": v(-252.34, 923.44) * mm, "end": v(-252.34, 930.94) * mm});
            skCircle(sketch, "E393", {"center": v(-252.34, 927.19) * mm, "radius": 2.07 * mm});
            skCircle(sketch, "E394", {"center": v(-252.34, 927.19) * mm, "radius": 2.5 * mm});
            skLineSegment(sketch, "E395", {"start": v(-248.6, 927.19) * mm, "end": v(-256.1, 927.19) * mm});
            skLineSegment(sketch, "E396", {"start": v(-252.34, 868.44) * mm, "end": v(-252.34, 875.94) * mm});
            skCircle(sketch, "E397", {"center": v(-252.34, 872.19) * mm, "radius": 2.07 * mm});
            skCircle(sketch, "E398", {"center": v(-252.34, 872.19) * mm, "radius": 2.5 * mm});
            skLineSegment(sketch, "E399", {"start": v(-248.6, 872.19) * mm, "end": v(-256.1, 872.19) * mm});
            skLineSegment(sketch, "E400", {"start": v(-252.34, 778.44) * mm, "end": v(-252.34, 785.94) * mm});
            skCircle(sketch, "E401", {"center": v(-252.34, 782.19) * mm, "radius": 2.07 * mm});
            skCircle(sketch, "E402", {"center": v(-252.34, 782.19) * mm, "radius": 2.5 * mm});
            skLineSegment(sketch, "E403", {"start": v(-248.6, 782.19) * mm, "end": v(-256.1, 782.19) * mm});
            skLineSegment(sketch, "E404", {"start": v(-252.34, 723.44) * mm, "end": v(-252.34, 730.94) * mm});
            skCircle(sketch, "E405", {"center": v(-252.34, 727.19) * mm, "radius": 2.07 * mm});
            skCircle(sketch, "E406", {"center": v(-252.34, 727.19) * mm, "radius": 2.5 * mm});
            skLineSegment(sketch, "E407", {"start": v(-248.6, 727.19) * mm, "end": v(-256.1, 727.19) * mm});
            skLineSegment(sketch, "E408", {"start": v(182.66, 778.44) * mm, "end": v(182.66, 785.94) * mm});
            skCircle(sketch, "E409", {"center": v(182.66, 782.19) * mm, "radius": 2.07 * mm});
            skCircle(sketch, "E410", {"center": v(182.66, 782.19) * mm, "radius": 2.5 * mm});
            skLineSegment(sketch, "E411", {"start": v(186.4, 782.19) * mm, "end": v(178.9, 782.19) * mm});
            skLineSegment(sketch, "E412", {"start": v(182.66, 723.44) * mm, "end": v(182.66, 730.94) * mm});
            skCircle(sketch, "E413", {"center": v(182.66, 727.19) * mm, "radius": 2.07 * mm});
            skCircle(sketch, "E414", {"center": v(182.66, 727.19) * mm, "radius": 2.5 * mm});
            skLineSegment(sketch, "E415", {"start": v(186.4, 727.19) * mm, "end": v(178.9, 727.19) * mm});
            skLineSegment(sketch, "E416", {"start": v(182.66, 923.44) * mm, "end": v(182.66, 930.94) * mm});
            skCircle(sketch, "E417", {"center": v(182.66, 927.19) * mm, "radius": 2.07 * mm});
            skCircle(sketch, "E418", {"center": v(182.66, 927.19) * mm, "radius": 2.5 * mm});
            skLineSegment(sketch, "E419", {"start": v(186.4, 927.19) * mm, "end": v(178.9, 927.19) * mm});
            skLineSegment(sketch, "E420", {"start": v(182.66, 868.44) * mm, "end": v(182.66, 875.94) * mm});
            skCircle(sketch, "E421", {"center": v(182.66, 872.19) * mm, "radius": 2.07 * mm});
            skCircle(sketch, "E422", {"center": v(182.66, 872.19) * mm, "radius": 2.5 * mm});
            skLineSegment(sketch, "E423", {"start": v(186.4, 872.19) * mm, "end": v(178.9, 872.19) * mm});
            skLineSegment(sketch, "E424.MirrorCS", {"start": v(182.66, 535.94) * mm, "end": v(182.66, 528.44) * mm});
            skLineSegment(sketch, "E425.MirrorCS", {"start": v(-252.34, 480.94) * mm, "end": v(-252.34, 473.44) * mm});
            skLineSegment(sketch, "E426.MirrorCS", {"start": v(182.66, 625.94) * mm, "end": v(182.66, 618.44) * mm});
            skCircle(sketch, "E427.MirrorC", {"center": v(-252.34, 532.19) * mm, "radius": 2.07 * mm});
            skCircle(sketch, "E428.MirrorC", {"center": v(182.66, 677.19) * mm, "radius": 2.07 * mm});
            skLineSegment(sketch, "E429.MirrorCS", {"start": v(-252.34, 680.94) * mm, "end": v(-252.34, 673.44) * mm});
            skCircle(sketch, "E430.MirrorC", {"center": v(-403.84, 534.69) * mm, "radius": 7 * mm});
            skLineSegment(sketch, "E431.MirrorCS", {"start": v(-394.74, 534.69) * mm, "end": v(-412.94, 534.69) * mm});
            skLineSegment(sketch, "E432.MirrorCS", {"start": v(-403.84, 543.79) * mm, "end": v(-403.84, 525.59) * mm});
            skCircle(sketch, "E433.MirrorC", {"center": v(182.66, 532.19) * mm, "radius": 2.07 * mm});
            skLineSegment(sketch, "E434.MirrorCS", {"start": v(182.66, 480.94) * mm, "end": v(182.66, 473.44) * mm});
            skCircle(sketch, "E435.MirrorC", {"center": v(182.66, 622.19) * mm, "radius": 2.07 * mm});
            skCircle(sketch, "E436.MirrorC", {"center": v(-252.34, 477.19) * mm, "radius": 2.07 * mm});
            skCircle(sketch, "E437.MirrorC", {"center": v(-252.34, 532.19) * mm, "radius": 2.5 * mm});
            skCircle(sketch, "E438.MirrorC", {"center": v(-252.34, 622.19) * mm, "radius": 2.07 * mm});
            skLineSegment(sketch, "E439.MirrorCS", {"start": v(-239.84, 687.19) * mm, "end": v(-264.84, 687.19) * mm});
            skLineSegment(sketch, "E440.MirrorCS", {"start": v(186.4, 532.19) * mm, "end": v(178.9, 532.19) * mm});
            skLineSegment(sketch, "E441.MirrorCS", {"start": v(-248.6, 677.19) * mm, "end": v(-256.1, 677.19) * mm});
            skCircle(sketch, "E442.MirrorC", {"center": v(-403.84, 534.69) * mm, "radius": 8.33 * mm});
            skLineSegment(sketch, "E443.MirrorCS", {"start": v(-239.84, 612.19) * mm, "end": v(-264.84, 612.19) * mm});
            skCircle(sketch, "E444.MirrorC", {"center": v(-252.34, 677.19) * mm, "radius": 2.07 * mm});
            skCircle(sketch, "E445.MirrorC", {"center": v(182.66, 532.19) * mm, "radius": 2.5 * mm});
            skLineSegment(sketch, "E446.MirrorCS", {"start": v(-239.84, 542.19) * mm, "end": v(-264.84, 542.19) * mm});
            skLineSegment(sketch, "E447.MirrorCS", {"start": v(-248.6, 622.19) * mm, "end": v(-256.1, 622.19) * mm});
            skLineSegment(sketch, "E448.MirrorCS", {"start": v(195.16, 542.19) * mm, "end": v(170.16, 542.19) * mm});
            skCircle(sketch, "E449.MirrorC", {"center": v(-252.34, 622.19) * mm, "radius": 2.5 * mm});
            skLineSegment(sketch, "E450.MirrorCS", {"start": v(186.4, 677.19) * mm, "end": v(178.9, 677.19) * mm});
            skLineSegment(sketch, "E451.MirrorCS", {"start": v(-248.6, 532.19) * mm, "end": v(-256.1, 532.19) * mm});
            skCircle(sketch, "E452.MirrorC", {"center": v(182.66, 477.19) * mm, "radius": 2.07 * mm});
            skLineSegment(sketch, "E453.MirrorCS", {"start": v(195.16, 612.19) * mm, "end": v(170.16, 612.19) * mm});
            skCircle(sketch, "E454.MirrorC", {"center": v(-252.34, 677.19) * mm, "radius": 2.5 * mm});
            skCircle(sketch, "E455.MirrorC", {"center": v(-403.84, 534.69) * mm, "radius": 7.56 * mm});
            skLineSegment(sketch, "E456.MirrorCS", {"start": v(195.16, 687.19) * mm, "end": v(170.16, 687.19) * mm});
            skLineSegment(sketch, "E457.MirrorCS", {"start": v(-252.34, 625.94) * mm, "end": v(-252.34, 618.44) * mm});
            skCircle(sketch, "E458.MirrorC", {"center": v(-403.84, 534.69) * mm, "radius": 11 * mm});
            skCircle(sketch, "E459.MirrorC", {"center": v(182.66, 622.19) * mm, "radius": 2.5 * mm});
            skCircle(sketch, "E460.MirrorC", {"center": v(-252.34, 477.19) * mm, "radius": 2.5 * mm});
            skCircle(sketch, "E461.MirrorC", {"center": v(182.66, 677.19) * mm, "radius": 2.5 * mm});
            skLineSegment(sketch, "E462.MirrorCS", {"start": v(-252.34, 535.94) * mm, "end": v(-252.34, 528.44) * mm});
            skLineSegment(sketch, "E463.MirrorCS", {"start": v(-248.6, 477.19) * mm, "end": v(-256.1, 477.19) * mm});
            skLineSegment(sketch, "E464.MirrorCS", {"start": v(186.4, 622.19) * mm, "end": v(178.9, 622.19) * mm});
            skLineSegment(sketch, "E465.MirrorCS", {"start": v(182.66, 680.94) * mm, "end": v(182.66, 673.44) * mm});
            skLineSegment(sketch, "E466.MirrorCS", {"start": v(-239.84, 467.19) * mm, "end": v(-264.84, 467.19) * mm});
            skLineSegment(sketch, "E467.MirrorCS", {"start": v(195.16, 467.19) * mm, "end": v(170.16, 467.19) * mm});
            skLineSegment(sketch, "E468.MirrorCS", {"start": v(186.4, 477.19) * mm, "end": v(178.9, 477.19) * mm});
            skCircle(sketch, "E469.MirrorC", {"center": v(182.66, 477.19) * mm, "radius": 2.5 * mm});
            skLineSegment(sketch, "E470.MirrorCS", {"start": v(170.16, 612.19) * mm, "end": v(170.16, 687.19) * mm});
            skLineSegment(sketch, "E471.MirrorCS", {"start": v(-421.54, 454.49) * mm, "end": v(-421.54, 699.89) * mm});
            skLineSegment(sketch, "E472.MirrorCS", {"start": v(170.16, 467.19) * mm, "end": v(170.16, 542.19) * mm});
            skLineSegment(sketch, "E473.MirrorCS", {"start": v(-421.54, 454.49) * mm, "end": v(341.86, 454.49) * mm});
            skLineSegment(sketch, "E474.MirrorCS", {"start": v(195.16, 612.19) * mm, "end": v(195.16, 687.19) * mm});
            skLineSegment(sketch, "E475.MirrorCS", {"start": v(-239.84, 467.19) * mm, "end": v(-239.84, 542.19) * mm});
            skLineSegment(sketch, "E476.MirrorCS", {"start": v(-239.84, 612.19) * mm, "end": v(-239.84, 687.19) * mm});
            skLineSegment(sketch, "E477.MirrorCS", {"start": v(-423.84, 452.19) * mm, "end": v(-423.84, 702.19) * mm});
            skLineSegment(sketch, "E478.MirrorCS", {"start": v(-423.84, 452.19) * mm, "end": v(344.16, 452.19) * mm});
            skLineSegment(sketch, "E479.MirrorCS", {"start": v(195.16, 467.19) * mm, "end": v(195.16, 542.19) * mm});
            skLineSegment(sketch, "E480.MirrorCS", {"start": v(-264.84, 467.19) * mm, "end": v(-264.84, 542.19) * mm});
            skLineSegment(sketch, "E481.MirrorCS", {"start": v(341.86, 454.49) * mm, "end": v(341.86, 699.89) * mm});
            skLineSegment(sketch, "E482.MirrorCS", {"start": v(-264.84, 612.19) * mm, "end": v(-264.84, 687.19) * mm});
            skPoint(sketch, "E483.orphan", {"position": v(-261, 542.19) * mm});
            skSolve(sketch);
        }
        {
            var Q0;
            Q0=makeQuery(id+"F0.imprint","IMPRINT",FACE,{"disambiguationData":[TD([[makeQuery(id+"F0.imprint","IMPRINT",EDGE,{"derivedFrom":sQuery(id+"F0.wireOp",EDGE,"E245")}),-1.0]])]});
            var Q1;
            Q1=makeQuery(id+"F0.imprint","IMPRINT",FACE,{"disambiguationData":[TD([[makeQuery(id+"F0.imprint","IMPRINT",EDGE,{"derivedFrom":sQuery(id+"F0.wireOp",EDGE,"E249")}),1.0]])]});
            var Q2;
            Q2=makeQuery(id+"F0.imprint","IMPRINT",FACE,{"disambiguationData":[TD([[makeQuery(id+"F0.imprint","IMPRINT",EDGE,{"derivedFrom":sQuery(id+"F0.wireOp",EDGE,"E248")}),1.0]])]});
            var Q3;
            Q3=makeQuery(id+"F0.imprint","IMPRINT",FACE,{"disambiguationData":[TD([[makeQuery(id+"F0.imprint","IMPRINT",EDGE,{"derivedFrom":sQuery(id+"F0.wireOp",EDGE,"E244")}),-1.0]])]});
            extrude(context, id + "F1", {"entities" : qUnion([Q0, Q1, Q2, Q3]), "depth" : 9 * mm});
        }
        {
            var Q0;
            Q0=makeQuery(id+"F0.imprint","IMPRINT",FACE,{"disambiguationData":[TD([[makeQuery(id+"F0.imprint","IMPRINT",EDGE,{"derivedFrom":sQuery(id+"F0.wireOp",EDGE,"E198")}),1.0]])]});
            extrude(context, id + "F2", {"entities" : qUnion([Q0]), "depth" : 20 * mm});
        }
        {
            var Q0;
            Q0=makeQuery(id+"F0.imprint","IMPRINT",FACE,{"disambiguationData":[TD([[makeQuery(id+"F0.imprint","IMPRINT",EDGE,{"derivedFrom":sQuery(id+"F0.wireOp",EDGE,"E199")}),1.0]])]});
            var Q1;
            Q1=makeQuery(id+"F0.imprint","IMPRINT",FACE,{"disambiguationData":[TD([[makeQuery(id+"F0.imprint","IMPRINT",EDGE,{"derivedFrom":sQuery(id+"F0.wireOp",EDGE,"E249")}),1.0]])]});
            var Q2;
            {var subQ0=sQuery(id+"F0.wireOp",EDGE,"E263");var subQ1=sQuery(id+"F0.wireOp",EDGE,"E260");var subQ2=makeQuery(id+"F0.imprint","INTERSECT",VERTEX,{"disambiguationData":[OD(0.0)],"derivedFrom":[subQ1,subQ0]});Q2=makeQuery(id+"F0.imprint","IMPRINT",FACE,{"disambiguationData":[TD([[makeQuery(id+"F0.imprint","IMPRINT",EDGE,{"disambiguationData":[TD([[subQ2,-1.0]])],"derivedFrom":subQ1}),1.0]])]});}
            var Q3;
            {var subQ0=sQuery(id+"F0.wireOp",EDGE,"E263");var subQ1=sQuery(id+"F0.wireOp",EDGE,"E260");var subQ2=makeQuery(id+"F0.imprint","INTERSECT",VERTEX,{"disambiguationData":[OD(0.0)],"derivedFrom":[subQ1,subQ0]});Q3=makeQuery(id+"F0.imprint","IMPRINT",FACE,{"disambiguationData":[TD([[makeQuery(id+"F0.imprint","IMPRINT",EDGE,{"disambiguationData":[TD([[subQ2,-1.0]])],"derivedFrom":subQ1}),-1.0]])]});}
            var Q4;
            {var subQ0=sQuery(id+"F0.wireOp",EDGE,"E262");var subQ1=sQuery(id+"F0.wireOp",EDGE,"E260");var subQ2=makeQuery(id+"F0.imprint","INTERSECT",VERTEX,{"derivedFrom":[subQ1,subQ0]});Q4=makeQuery(id+"F0.imprint","IMPRINT",FACE,{"disambiguationData":[TD([[makeQuery(id+"F0.imprint","IMPRINT",EDGE,{"disambiguationData":[TD([[subQ2,-1.0]])],"derivedFrom":subQ1}),1.0]])]});}
            var Q5;
            {var subQ0=sQuery(id+"F0.wireOp",EDGE,"E262");var subQ1=sQuery(id+"F0.wireOp",EDGE,"E260");var subQ2=makeQuery(id+"F0.imprint","INTERSECT",VERTEX,{"derivedFrom":[subQ1,subQ0]});Q5=makeQuery(id+"F0.imprint","IMPRINT",FACE,{"disambiguationData":[TD([[makeQuery(id+"F0.imprint","IMPRINT",EDGE,{"disambiguationData":[TD([[subQ2,-1.0]])],"derivedFrom":subQ1}),-1.0]])]});}
            var Q6;
            {var subQ0=sQuery(id+"F0.wireOp",EDGE,"E261");var subQ1=sQuery(id+"F0.wireOp",EDGE,"E260");var subQ2=makeQuery(id+"F0.imprint","INTERSECT",VERTEX,{"disambiguationData":[OD(0.0)],"derivedFrom":[subQ1,subQ0]});Q6=makeQuery(id+"F0.imprint","IMPRINT",FACE,{"disambiguationData":[TD([[makeQuery(id+"F0.imprint","IMPRINT",EDGE,{"disambiguationData":[TD([[subQ2,-1.0]])],"derivedFrom":subQ1}),-1.0]])]});}
            var Q7;
            {var subQ0=sQuery(id+"F0.wireOp",EDGE,"E261");var subQ1=sQuery(id+"F0.wireOp",EDGE,"E260");var subQ2=makeQuery(id+"F0.imprint","INTERSECT",VERTEX,{"disambiguationData":[OD(1.0)],"derivedFrom":[subQ1,subQ0]});Q7=makeQuery(id+"F0.imprint","IMPRINT",FACE,{"disambiguationData":[TD([[makeQuery(id+"F0.imprint","IMPRINT",EDGE,{"disambiguationData":[TD([[subQ2,1.0]])],"derivedFrom":subQ1}),1.0]])]});}
            var Q8;
            {var subQ0=sQuery(id+"F0.wireOp",EDGE,"E261");var subQ1=sQuery(id+"F0.wireOp",EDGE,"E260");var subQ2=makeQuery(id+"F0.imprint","INTERSECT",VERTEX,{"disambiguationData":[OD(0.0)],"derivedFrom":[subQ1,subQ0]});Q8=makeQuery(id+"F0.imprint","IMPRINT",FACE,{"disambiguationData":[TD([[makeQuery(id+"F0.imprint","IMPRINT",EDGE,{"disambiguationData":[TD([[subQ2,-1.0]])],"derivedFrom":subQ1}),1.0]])]});}
            var Q9;
            {var subQ0=sQuery(id+"F0.wireOp",EDGE,"E261");var subQ1=sQuery(id+"F0.wireOp",EDGE,"E260");var subQ2=makeQuery(id+"F0.imprint","INTERSECT",VERTEX,{"disambiguationData":[OD(1.0)],"derivedFrom":[subQ1,subQ0]});Q9=makeQuery(id+"F0.imprint","IMPRINT",FACE,{"disambiguationData":[TD([[makeQuery(id+"F0.imprint","IMPRINT",EDGE,{"disambiguationData":[TD([[subQ2,1.0]])],"derivedFrom":subQ1}),-1.0]])]});}
            var Q10;
            Q10=makeQuery(id+"F1.opExtrude","CAP_FACE",FACE,{"disambiguationData":[OSD([sQuery(id+"F0.wireOp",EDGE,"E249"),sQuery(id+"F0.wireOp",EDGE,"E251"),sQuery(id+"F0.wireOp",EDGE,"E256"),sQuery(id+"F0.wireOp",EDGE,"E258"),sQuery(id+"F0.wireOp",EDGE,"E261"),sQuery(id+"F0.wireOp",EDGE,"E269")])],"isStart":true});
            var Q11;
            {var subQ0=sQuery(id+"F0.wireOp",EDGE,"E269");var subQ1=sQuery(id+"F0.wireOp",EDGE,"E268");var subQ2=makeQuery(id+"F0.imprint","INTERSECT",VERTEX,{"disambiguationData":[OD(1.0)],"derivedFrom":[subQ1,subQ0]});Q11=makeQuery(id+"F0.imprint","IMPRINT",FACE,{"disambiguationData":[TD([[makeQuery(id+"F0.imprint","IMPRINT",EDGE,{"disambiguationData":[TD([[subQ2,1.0]])],"derivedFrom":subQ1}),-1.0]])]});}
            var Q12;
            {var subQ0=sQuery(id+"F0.wireOp",EDGE,"E269");var subQ1=sQuery(id+"F0.wireOp",EDGE,"E268");var subQ2=makeQuery(id+"F0.imprint","INTERSECT",VERTEX,{"disambiguationData":[OD(1.0)],"derivedFrom":[subQ1,subQ0]});Q12=makeQuery(id+"F0.imprint","IMPRINT",FACE,{"disambiguationData":[TD([[makeQuery(id+"F0.imprint","IMPRINT",EDGE,{"disambiguationData":[TD([[subQ2,1.0]])],"derivedFrom":subQ1}),1.0]])]});}
            var Q13;
            {var subQ0=sQuery(id+"F0.wireOp",EDGE,"E270");var subQ1=sQuery(id+"F0.wireOp",EDGE,"E268");var subQ2=makeQuery(id+"F0.imprint","INTERSECT",VERTEX,{"derivedFrom":[subQ1,subQ0]});Q13=makeQuery(id+"F0.imprint","IMPRINT",FACE,{"disambiguationData":[TD([[makeQuery(id+"F0.imprint","IMPRINT",EDGE,{"disambiguationData":[TD([[subQ2,-1.0]])],"derivedFrom":subQ1}),1.0]])]});}
            var Q14;
            {var subQ0=sQuery(id+"F0.wireOp",EDGE,"E270");var subQ1=sQuery(id+"F0.wireOp",EDGE,"E268");var subQ2=makeQuery(id+"F0.imprint","INTERSECT",VERTEX,{"derivedFrom":[subQ1,subQ0]});Q14=makeQuery(id+"F0.imprint","IMPRINT",FACE,{"disambiguationData":[TD([[makeQuery(id+"F0.imprint","IMPRINT",EDGE,{"disambiguationData":[TD([[subQ2,-1.0]])],"derivedFrom":subQ1}),-1.0]])]});}
            var Q15;
            {var subQ0=sQuery(id+"F0.wireOp",EDGE,"E271");var subQ1=sQuery(id+"F0.wireOp",EDGE,"E268");var subQ2=makeQuery(id+"F0.imprint","INTERSECT",VERTEX,{"disambiguationData":[OD(0.0)],"derivedFrom":[subQ1,subQ0]});Q15=makeQuery(id+"F0.imprint","IMPRINT",FACE,{"disambiguationData":[TD([[makeQuery(id+"F0.imprint","IMPRINT",EDGE,{"disambiguationData":[TD([[subQ2,-1.0]])],"derivedFrom":subQ1}),-1.0]])]});}
            var Q16;
            {var subQ0=sQuery(id+"F0.wireOp",EDGE,"E271");var subQ1=sQuery(id+"F0.wireOp",EDGE,"E268");var subQ2=makeQuery(id+"F0.imprint","INTERSECT",VERTEX,{"disambiguationData":[OD(0.0)],"derivedFrom":[subQ1,subQ0]});Q16=makeQuery(id+"F0.imprint","IMPRINT",FACE,{"disambiguationData":[TD([[makeQuery(id+"F0.imprint","IMPRINT",EDGE,{"disambiguationData":[TD([[subQ2,-1.0]])],"derivedFrom":subQ1}),1.0]])]});}
            var Q17;
            {var subQ0=sQuery(id+"F0.wireOp",EDGE,"E269");var subQ1=sQuery(id+"F0.wireOp",EDGE,"E268");var subQ2=makeQuery(id+"F0.imprint","INTERSECT",VERTEX,{"disambiguationData":[OD(0.0)],"derivedFrom":[subQ1,subQ0]});Q17=makeQuery(id+"F0.imprint","IMPRINT",FACE,{"disambiguationData":[TD([[makeQuery(id+"F0.imprint","IMPRINT",EDGE,{"disambiguationData":[TD([[subQ2,-1.0]])],"derivedFrom":subQ1}),-1.0]])]});}
            var Q18;
            {var subQ0=sQuery(id+"F0.wireOp",EDGE,"E269");var subQ1=sQuery(id+"F0.wireOp",EDGE,"E268");var subQ2=makeQuery(id+"F0.imprint","INTERSECT",VERTEX,{"disambiguationData":[OD(0.0)],"derivedFrom":[subQ1,subQ0]});Q18=makeQuery(id+"F0.imprint","IMPRINT",FACE,{"disambiguationData":[TD([[makeQuery(id+"F0.imprint","IMPRINT",EDGE,{"disambiguationData":[TD([[subQ2,-1.0]])],"derivedFrom":subQ1}),1.0]])]});}
            var Q19;
            Q19=makeQuery(id+"F0.imprint","IMPRINT",FACE,{"disambiguationData":[TD([[makeQuery(id+"F0.imprint","IMPRINT",EDGE,{"derivedFrom":sQuery(id+"F0.wireOp",EDGE,"E248")}),1.0]])]});
            var Q20;
            {var subQ0=sQuery(id+"F0.wireOp",EDGE,"E285");var subQ1=sQuery(id+"F0.wireOp",EDGE,"E284");var subQ2=makeQuery(id+"F0.imprint","INTERSECT",VERTEX,{"disambiguationData":[OD(0.0)],"derivedFrom":[subQ1,subQ0]});Q20=makeQuery(id+"F0.imprint","IMPRINT",FACE,{"disambiguationData":[TD([[makeQuery(id+"F0.imprint","IMPRINT",EDGE,{"disambiguationData":[TD([[subQ2,-1.0]])],"derivedFrom":subQ1}),1.0]])]});}
            var Q21;
            {var subQ0=sQuery(id+"F0.wireOp",EDGE,"E286");var subQ1=sQuery(id+"F0.wireOp",EDGE,"E284");var subQ2=makeQuery(id+"F0.imprint","INTERSECT",VERTEX,{"derivedFrom":[subQ1,subQ0]});Q21=makeQuery(id+"F0.imprint","IMPRINT",FACE,{"disambiguationData":[TD([[makeQuery(id+"F0.imprint","IMPRINT",EDGE,{"disambiguationData":[TD([[subQ2,-1.0]])],"derivedFrom":subQ1}),1.0]])]});}
            var Q22;
            {var subQ0=sQuery(id+"F0.wireOp",EDGE,"E285");var subQ1=sQuery(id+"F0.wireOp",EDGE,"E284");var subQ2=makeQuery(id+"F0.imprint","INTERSECT",VERTEX,{"disambiguationData":[OD(1.0)],"derivedFrom":[subQ1,subQ0]});Q22=makeQuery(id+"F0.imprint","IMPRINT",FACE,{"disambiguationData":[TD([[makeQuery(id+"F0.imprint","IMPRINT",EDGE,{"disambiguationData":[TD([[subQ2,1.0]])],"derivedFrom":subQ1}),1.0]])]});}
            var Q23;
            {var subQ0=sQuery(id+"F0.wireOp",EDGE,"E286");var subQ1=sQuery(id+"F0.wireOp",EDGE,"E284");var subQ2=makeQuery(id+"F0.imprint","INTERSECT",VERTEX,{"derivedFrom":[subQ1,subQ0]});Q23=makeQuery(id+"F0.imprint","IMPRINT",FACE,{"disambiguationData":[TD([[makeQuery(id+"F0.imprint","IMPRINT",EDGE,{"disambiguationData":[TD([[subQ2,-1.0]])],"derivedFrom":subQ1}),-1.0]])]});}
            var Q24;
            {var subQ0=sQuery(id+"F0.wireOp",EDGE,"E285");var subQ1=sQuery(id+"F0.wireOp",EDGE,"E284");var subQ2=makeQuery(id+"F0.imprint","INTERSECT",VERTEX,{"disambiguationData":[OD(1.0)],"derivedFrom":[subQ1,subQ0]});Q24=makeQuery(id+"F0.imprint","IMPRINT",FACE,{"disambiguationData":[TD([[makeQuery(id+"F0.imprint","IMPRINT",EDGE,{"disambiguationData":[TD([[subQ2,1.0]])],"derivedFrom":subQ1}),-1.0]])]});}
            var Q25;
            {var subQ0=sQuery(id+"F0.wireOp",EDGE,"E285");var subQ1=sQuery(id+"F0.wireOp",EDGE,"E284");var subQ2=makeQuery(id+"F0.imprint","INTERSECT",VERTEX,{"disambiguationData":[OD(0.0)],"derivedFrom":[subQ1,subQ0]});Q25=makeQuery(id+"F0.imprint","IMPRINT",FACE,{"disambiguationData":[TD([[makeQuery(id+"F0.imprint","IMPRINT",EDGE,{"disambiguationData":[TD([[subQ2,-1.0]])],"derivedFrom":subQ1}),-1.0]])]});}
            var Q26;
            {var subQ0=sQuery(id+"F0.wireOp",EDGE,"E287");var subQ1=sQuery(id+"F0.wireOp",EDGE,"E284");var subQ2=makeQuery(id+"F0.imprint","INTERSECT",VERTEX,{"disambiguationData":[OD(0.0)],"derivedFrom":[subQ1,subQ0]});Q26=makeQuery(id+"F0.imprint","IMPRINT",FACE,{"disambiguationData":[TD([[makeQuery(id+"F0.imprint","IMPRINT",EDGE,{"disambiguationData":[TD([[subQ2,-1.0]])],"derivedFrom":subQ1}),-1.0]])]});}
            var Q27;
            {var subQ0=sQuery(id+"F0.wireOp",EDGE,"E287");var subQ1=sQuery(id+"F0.wireOp",EDGE,"E284");var subQ2=makeQuery(id+"F0.imprint","INTERSECT",VERTEX,{"disambiguationData":[OD(0.0)],"derivedFrom":[subQ1,subQ0]});Q27=makeQuery(id+"F0.imprint","IMPRINT",FACE,{"disambiguationData":[TD([[makeQuery(id+"F0.imprint","IMPRINT",EDGE,{"disambiguationData":[TD([[subQ2,-1.0]])],"derivedFrom":subQ1}),1.0]])]});}
            var Q28;
            {var subQ0=sQuery(id+"F0.wireOp",EDGE,"E279");var subQ1=sQuery(id+"F0.wireOp",EDGE,"E276");var subQ2=makeQuery(id+"F0.imprint","INTERSECT",VERTEX,{"disambiguationData":[OD(0.0)],"derivedFrom":[subQ1,subQ0]});Q28=makeQuery(id+"F0.imprint","IMPRINT",FACE,{"disambiguationData":[TD([[makeQuery(id+"F0.imprint","IMPRINT",EDGE,{"disambiguationData":[TD([[subQ2,-1.0]])],"derivedFrom":subQ1}),1.0]])]});}
            var Q29;
            {var subQ0=sQuery(id+"F0.wireOp",EDGE,"E278");var subQ1=sQuery(id+"F0.wireOp",EDGE,"E276");var subQ2=makeQuery(id+"F0.imprint","INTERSECT",VERTEX,{"derivedFrom":[subQ1,subQ0]});Q29=makeQuery(id+"F0.imprint","IMPRINT",FACE,{"disambiguationData":[TD([[makeQuery(id+"F0.imprint","IMPRINT",EDGE,{"disambiguationData":[TD([[subQ2,-1.0]])],"derivedFrom":subQ1}),1.0]])]});}
            var Q30;
            {var subQ0=sQuery(id+"F0.wireOp",EDGE,"E278");var subQ1=sQuery(id+"F0.wireOp",EDGE,"E276");var subQ2=makeQuery(id+"F0.imprint","INTERSECT",VERTEX,{"derivedFrom":[subQ1,subQ0]});Q30=makeQuery(id+"F0.imprint","IMPRINT",FACE,{"disambiguationData":[TD([[makeQuery(id+"F0.imprint","IMPRINT",EDGE,{"disambiguationData":[TD([[subQ2,-1.0]])],"derivedFrom":subQ1}),-1.0]])]});}
            var Q31;
            {var subQ0=sQuery(id+"F0.wireOp",EDGE,"E279");var subQ1=sQuery(id+"F0.wireOp",EDGE,"E276");var subQ2=makeQuery(id+"F0.imprint","INTERSECT",VERTEX,{"disambiguationData":[OD(0.0)],"derivedFrom":[subQ1,subQ0]});Q31=makeQuery(id+"F0.imprint","IMPRINT",FACE,{"disambiguationData":[TD([[makeQuery(id+"F0.imprint","IMPRINT",EDGE,{"disambiguationData":[TD([[subQ2,-1.0]])],"derivedFrom":subQ1}),-1.0]])]});}
            var Q32;
            {var subQ0=sQuery(id+"F0.wireOp",EDGE,"E277");var subQ1=sQuery(id+"F0.wireOp",EDGE,"E276");var subQ2=makeQuery(id+"F0.imprint","INTERSECT",VERTEX,{"disambiguationData":[OD(0.0)],"derivedFrom":[subQ1,subQ0]});Q32=makeQuery(id+"F0.imprint","IMPRINT",FACE,{"disambiguationData":[TD([[makeQuery(id+"F0.imprint","IMPRINT",EDGE,{"disambiguationData":[TD([[subQ2,-1.0]])],"derivedFrom":subQ1}),1.0]])]});}
            var Q33;
            {var subQ0=sQuery(id+"F0.wireOp",EDGE,"E277");var subQ1=sQuery(id+"F0.wireOp",EDGE,"E276");var subQ2=makeQuery(id+"F0.imprint","INTERSECT",VERTEX,{"disambiguationData":[OD(1.0)],"derivedFrom":[subQ1,subQ0]});Q33=makeQuery(id+"F0.imprint","IMPRINT",FACE,{"disambiguationData":[TD([[makeQuery(id+"F0.imprint","IMPRINT",EDGE,{"disambiguationData":[TD([[subQ2,1.0]])],"derivedFrom":subQ1}),1.0]])]});}
            var Q34;
            {var subQ0=sQuery(id+"F0.wireOp",EDGE,"E277");var subQ1=sQuery(id+"F0.wireOp",EDGE,"E276");var subQ2=makeQuery(id+"F0.imprint","INTERSECT",VERTEX,{"disambiguationData":[OD(1.0)],"derivedFrom":[subQ1,subQ0]});Q34=makeQuery(id+"F0.imprint","IMPRINT",FACE,{"disambiguationData":[TD([[makeQuery(id+"F0.imprint","IMPRINT",EDGE,{"disambiguationData":[TD([[subQ2,1.0]])],"derivedFrom":subQ1}),-1.0]])]});}
            var Q35;
            {var subQ0=sQuery(id+"F0.wireOp",EDGE,"E277");var subQ1=sQuery(id+"F0.wireOp",EDGE,"E276");var subQ2=makeQuery(id+"F0.imprint","INTERSECT",VERTEX,{"disambiguationData":[OD(0.0)],"derivedFrom":[subQ1,subQ0]});Q35=makeQuery(id+"F0.imprint","IMPRINT",FACE,{"disambiguationData":[TD([[makeQuery(id+"F0.imprint","IMPRINT",EDGE,{"disambiguationData":[TD([[subQ2,-1.0]])],"derivedFrom":subQ1}),-1.0]])]});}
            var Q36;
            Q36=makeQuery(id+"F0.imprint","IMPRINT",FACE,{"disambiguationData":[TD([[makeQuery(id+"F0.imprint","IMPRINT",EDGE,{"derivedFrom":sQuery(id+"F0.wireOp",EDGE,"E245")}),-1.0]])]});
            var Q37;
            Q37=makeQuery(id+"F0.imprint","IMPRINT",FACE,{"disambiguationData":[TD([[makeQuery(id+"F0.imprint","IMPRINT",EDGE,{"derivedFrom":sQuery(id+"F0.wireOp",EDGE,"E244")}),-1.0]])]});
            var Q38;
            {var subQ0=sQuery(id+"F0.wireOp",EDGE,"E273");var subQ1=sQuery(id+"F0.wireOp",EDGE,"E272");var subQ2=makeQuery(id+"F0.imprint","INTERSECT",VERTEX,{"disambiguationData":[OD(0.0)],"derivedFrom":[subQ1,subQ0]});Q38=makeQuery(id+"F0.imprint","IMPRINT",FACE,{"disambiguationData":[TD([[makeQuery(id+"F0.imprint","IMPRINT",EDGE,{"disambiguationData":[TD([[subQ2,-1.0]])],"derivedFrom":subQ1}),1.0]])]});}
            var Q39;
            {var subQ0=sQuery(id+"F0.wireOp",EDGE,"E273");var subQ1=sQuery(id+"F0.wireOp",EDGE,"E272");var subQ2=makeQuery(id+"F0.imprint","INTERSECT",VERTEX,{"disambiguationData":[OD(1.0)],"derivedFrom":[subQ1,subQ0]});Q39=makeQuery(id+"F0.imprint","IMPRINT",FACE,{"disambiguationData":[TD([[makeQuery(id+"F0.imprint","IMPRINT",EDGE,{"disambiguationData":[TD([[subQ2,1.0]])],"derivedFrom":subQ1}),1.0]])]});}
            var Q40;
            {var subQ0=sQuery(id+"F0.wireOp",EDGE,"E274");var subQ1=sQuery(id+"F0.wireOp",EDGE,"E272");var subQ2=makeQuery(id+"F0.imprint","INTERSECT",VERTEX,{"derivedFrom":[subQ1,subQ0]});Q40=makeQuery(id+"F0.imprint","IMPRINT",FACE,{"disambiguationData":[TD([[makeQuery(id+"F0.imprint","IMPRINT",EDGE,{"disambiguationData":[TD([[subQ2,-1.0]])],"derivedFrom":subQ1}),1.0]])]});}
            var Q41;
            {var subQ0=sQuery(id+"F0.wireOp",EDGE,"E275");var subQ1=sQuery(id+"F0.wireOp",EDGE,"E272");var subQ2=makeQuery(id+"F0.imprint","INTERSECT",VERTEX,{"disambiguationData":[OD(0.0)],"derivedFrom":[subQ1,subQ0]});Q41=makeQuery(id+"F0.imprint","IMPRINT",FACE,{"disambiguationData":[TD([[makeQuery(id+"F0.imprint","IMPRINT",EDGE,{"disambiguationData":[TD([[subQ2,-1.0]])],"derivedFrom":subQ1}),1.0]])]});}
            var Q42;
            {var subQ0=sQuery(id+"F0.wireOp",EDGE,"E275");var subQ1=sQuery(id+"F0.wireOp",EDGE,"E272");var subQ2=makeQuery(id+"F0.imprint","INTERSECT",VERTEX,{"disambiguationData":[OD(0.0)],"derivedFrom":[subQ1,subQ0]});Q42=makeQuery(id+"F0.imprint","IMPRINT",FACE,{"disambiguationData":[TD([[makeQuery(id+"F0.imprint","IMPRINT",EDGE,{"disambiguationData":[TD([[subQ2,-1.0]])],"derivedFrom":subQ1}),-1.0]])]});}
            var Q43;
            {var subQ0=sQuery(id+"F0.wireOp",EDGE,"E273");var subQ1=sQuery(id+"F0.wireOp",EDGE,"E272");var subQ2=makeQuery(id+"F0.imprint","INTERSECT",VERTEX,{"disambiguationData":[OD(1.0)],"derivedFrom":[subQ1,subQ0]});Q43=makeQuery(id+"F0.imprint","IMPRINT",FACE,{"disambiguationData":[TD([[makeQuery(id+"F0.imprint","IMPRINT",EDGE,{"disambiguationData":[TD([[subQ2,1.0]])],"derivedFrom":subQ1}),-1.0]])]});}
            var Q44;
            {var subQ0=sQuery(id+"F0.wireOp",EDGE,"E274");var subQ1=sQuery(id+"F0.wireOp",EDGE,"E272");var subQ2=makeQuery(id+"F0.imprint","INTERSECT",VERTEX,{"derivedFrom":[subQ1,subQ0]});Q44=makeQuery(id+"F0.imprint","IMPRINT",FACE,{"disambiguationData":[TD([[makeQuery(id+"F0.imprint","IMPRINT",EDGE,{"disambiguationData":[TD([[subQ2,-1.0]])],"derivedFrom":subQ1}),-1.0]])]});}
            var Q45;
            {var subQ0=sQuery(id+"F0.wireOp",EDGE,"E273");var subQ1=sQuery(id+"F0.wireOp",EDGE,"E272");var subQ2=makeQuery(id+"F0.imprint","INTERSECT",VERTEX,{"disambiguationData":[OD(0.0)],"derivedFrom":[subQ1,subQ0]});Q45=makeQuery(id+"F0.imprint","IMPRINT",FACE,{"disambiguationData":[TD([[makeQuery(id+"F0.imprint","IMPRINT",EDGE,{"disambiguationData":[TD([[subQ2,-1.0]])],"derivedFrom":subQ1}),-1.0]])]});}
            var Q46;
            {var subQ0=sQuery(id+"F0.wireOp",EDGE,"E265");var subQ1=sQuery(id+"F0.wireOp",EDGE,"E264");var subQ2=makeQuery(id+"F0.imprint","INTERSECT",VERTEX,{"disambiguationData":[OD(0.0)],"derivedFrom":[subQ1,subQ0]});Q46=makeQuery(id+"F0.imprint","IMPRINT",FACE,{"disambiguationData":[TD([[makeQuery(id+"F0.imprint","IMPRINT",EDGE,{"disambiguationData":[TD([[subQ2,-1.0]])],"derivedFrom":subQ1}),1.0]])]});}
            var Q47;
            {var subQ0=sQuery(id+"F0.wireOp",EDGE,"E267");var subQ1=sQuery(id+"F0.wireOp",EDGE,"E264");var subQ2=makeQuery(id+"F0.imprint","INTERSECT",VERTEX,{"disambiguationData":[OD(0.0)],"derivedFrom":[subQ1,subQ0]});Q47=makeQuery(id+"F0.imprint","IMPRINT",FACE,{"disambiguationData":[TD([[makeQuery(id+"F0.imprint","IMPRINT",EDGE,{"disambiguationData":[TD([[subQ2,-1.0]])],"derivedFrom":subQ1}),1.0]])]});}
            var Q48;
            {var subQ0=sQuery(id+"F0.wireOp",EDGE,"E266");var subQ1=sQuery(id+"F0.wireOp",EDGE,"E264");var subQ2=makeQuery(id+"F0.imprint","INTERSECT",VERTEX,{"derivedFrom":[subQ1,subQ0]});Q48=makeQuery(id+"F0.imprint","IMPRINT",FACE,{"disambiguationData":[TD([[makeQuery(id+"F0.imprint","IMPRINT",EDGE,{"disambiguationData":[TD([[subQ2,-1.0]])],"derivedFrom":subQ1}),1.0]])]});}
            var Q49;
            {var subQ0=sQuery(id+"F0.wireOp",EDGE,"E265");var subQ1=sQuery(id+"F0.wireOp",EDGE,"E264");var subQ2=makeQuery(id+"F0.imprint","INTERSECT",VERTEX,{"disambiguationData":[OD(1.0)],"derivedFrom":[subQ1,subQ0]});Q49=makeQuery(id+"F0.imprint","IMPRINT",FACE,{"disambiguationData":[TD([[makeQuery(id+"F0.imprint","IMPRINT",EDGE,{"disambiguationData":[TD([[subQ2,1.0]])],"derivedFrom":subQ1}),1.0]])]});}
            var Q50;
            {var subQ0=sQuery(id+"F0.wireOp",EDGE,"E265");var subQ1=sQuery(id+"F0.wireOp",EDGE,"E264");var subQ2=makeQuery(id+"F0.imprint","INTERSECT",VERTEX,{"disambiguationData":[OD(1.0)],"derivedFrom":[subQ1,subQ0]});Q50=makeQuery(id+"F0.imprint","IMPRINT",FACE,{"disambiguationData":[TD([[makeQuery(id+"F0.imprint","IMPRINT",EDGE,{"disambiguationData":[TD([[subQ2,1.0]])],"derivedFrom":subQ1}),-1.0]])]});}
            var Q51;
            {var subQ0=sQuery(id+"F0.wireOp",EDGE,"E266");var subQ1=sQuery(id+"F0.wireOp",EDGE,"E264");var subQ2=makeQuery(id+"F0.imprint","INTERSECT",VERTEX,{"derivedFrom":[subQ1,subQ0]});Q51=makeQuery(id+"F0.imprint","IMPRINT",FACE,{"disambiguationData":[TD([[makeQuery(id+"F0.imprint","IMPRINT",EDGE,{"disambiguationData":[TD([[subQ2,-1.0]])],"derivedFrom":subQ1}),-1.0]])]});}
            var Q52;
            {var subQ0=sQuery(id+"F0.wireOp",EDGE,"E267");var subQ1=sQuery(id+"F0.wireOp",EDGE,"E264");var subQ2=makeQuery(id+"F0.imprint","INTERSECT",VERTEX,{"disambiguationData":[OD(0.0)],"derivedFrom":[subQ1,subQ0]});Q52=makeQuery(id+"F0.imprint","IMPRINT",FACE,{"disambiguationData":[TD([[makeQuery(id+"F0.imprint","IMPRINT",EDGE,{"disambiguationData":[TD([[subQ2,-1.0]])],"derivedFrom":subQ1}),-1.0]])]});}
            var Q53;
            {var subQ0=sQuery(id+"F0.wireOp",EDGE,"E265");var subQ1=sQuery(id+"F0.wireOp",EDGE,"E264");var subQ2=makeQuery(id+"F0.imprint","INTERSECT",VERTEX,{"disambiguationData":[OD(0.0)],"derivedFrom":[subQ1,subQ0]});Q53=makeQuery(id+"F0.imprint","IMPRINT",FACE,{"disambiguationData":[TD([[makeQuery(id+"F0.imprint","IMPRINT",EDGE,{"disambiguationData":[TD([[subQ2,-1.0]])],"derivedFrom":subQ1}),-1.0]])]});}
            var Q54;
            {var subQ0=sQuery(id+"F0.wireOp",EDGE,"E289");var subQ1=sQuery(id+"F0.wireOp",EDGE,"E288");var subQ2=makeQuery(id+"F0.imprint","INTERSECT",VERTEX,{"disambiguationData":[OD(0.0)],"derivedFrom":[subQ1,subQ0]});Q54=makeQuery(id+"F0.imprint","IMPRINT",FACE,{"disambiguationData":[TD([[makeQuery(id+"F0.imprint","IMPRINT",EDGE,{"disambiguationData":[TD([[subQ2,-1.0]])],"derivedFrom":subQ1}),1.0]])]});}
            var Q55;
            {var subQ0=sQuery(id+"F0.wireOp",EDGE,"E289");var subQ1=sQuery(id+"F0.wireOp",EDGE,"E288");var subQ2=makeQuery(id+"F0.imprint","INTERSECT",VERTEX,{"disambiguationData":[OD(1.0)],"derivedFrom":[subQ1,subQ0]});Q55=makeQuery(id+"F0.imprint","IMPRINT",FACE,{"disambiguationData":[TD([[makeQuery(id+"F0.imprint","IMPRINT",EDGE,{"disambiguationData":[TD([[subQ2,1.0]])],"derivedFrom":subQ1}),1.0]])]});}
            var Q56;
            {var subQ0=sQuery(id+"F0.wireOp",EDGE,"E290");var subQ1=sQuery(id+"F0.wireOp",EDGE,"E288");var subQ2=makeQuery(id+"F0.imprint","INTERSECT",VERTEX,{"derivedFrom":[subQ1,subQ0]});Q56=makeQuery(id+"F0.imprint","IMPRINT",FACE,{"disambiguationData":[TD([[makeQuery(id+"F0.imprint","IMPRINT",EDGE,{"disambiguationData":[TD([[subQ2,-1.0]])],"derivedFrom":subQ1}),1.0]])]});}
            var Q57;
            {var subQ0=sQuery(id+"F0.wireOp",EDGE,"E291");var subQ1=sQuery(id+"F0.wireOp",EDGE,"E288");var subQ2=makeQuery(id+"F0.imprint","INTERSECT",VERTEX,{"disambiguationData":[OD(0.0)],"derivedFrom":[subQ1,subQ0]});Q57=makeQuery(id+"F0.imprint","IMPRINT",FACE,{"disambiguationData":[TD([[makeQuery(id+"F0.imprint","IMPRINT",EDGE,{"disambiguationData":[TD([[subQ2,-1.0]])],"derivedFrom":subQ1}),1.0]])]});}
            var Q58;
            {var subQ0=sQuery(id+"F0.wireOp",EDGE,"E290");var subQ1=sQuery(id+"F0.wireOp",EDGE,"E288");var subQ2=makeQuery(id+"F0.imprint","INTERSECT",VERTEX,{"derivedFrom":[subQ1,subQ0]});Q58=makeQuery(id+"F0.imprint","IMPRINT",FACE,{"disambiguationData":[TD([[makeQuery(id+"F0.imprint","IMPRINT",EDGE,{"disambiguationData":[TD([[subQ2,-1.0]])],"derivedFrom":subQ1}),-1.0]])]});}
            var Q59;
            {var subQ0=sQuery(id+"F0.wireOp",EDGE,"E289");var subQ1=sQuery(id+"F0.wireOp",EDGE,"E288");var subQ2=makeQuery(id+"F0.imprint","INTERSECT",VERTEX,{"disambiguationData":[OD(1.0)],"derivedFrom":[subQ1,subQ0]});Q59=makeQuery(id+"F0.imprint","IMPRINT",FACE,{"disambiguationData":[TD([[makeQuery(id+"F0.imprint","IMPRINT",EDGE,{"disambiguationData":[TD([[subQ2,1.0]])],"derivedFrom":subQ1}),-1.0]])]});}
            var Q60;
            {var subQ0=sQuery(id+"F0.wireOp",EDGE,"E291");var subQ1=sQuery(id+"F0.wireOp",EDGE,"E288");var subQ2=makeQuery(id+"F0.imprint","INTERSECT",VERTEX,{"disambiguationData":[OD(0.0)],"derivedFrom":[subQ1,subQ0]});Q60=makeQuery(id+"F0.imprint","IMPRINT",FACE,{"disambiguationData":[TD([[makeQuery(id+"F0.imprint","IMPRINT",EDGE,{"disambiguationData":[TD([[subQ2,-1.0]])],"derivedFrom":subQ1}),-1.0]])]});}
            var Q61;
            {var subQ0=sQuery(id+"F0.wireOp",EDGE,"E289");var subQ1=sQuery(id+"F0.wireOp",EDGE,"E288");var subQ2=makeQuery(id+"F0.imprint","INTERSECT",VERTEX,{"disambiguationData":[OD(0.0)],"derivedFrom":[subQ1,subQ0]});Q61=makeQuery(id+"F0.imprint","IMPRINT",FACE,{"disambiguationData":[TD([[makeQuery(id+"F0.imprint","IMPRINT",EDGE,{"disambiguationData":[TD([[subQ2,-1.0]])],"derivedFrom":subQ1}),-1.0]])]});}
            var Q62;
            {var subQ0=sQuery(id+"F0.wireOp",EDGE,"E281");var subQ1=sQuery(id+"F0.wireOp",EDGE,"E280");var subQ2=makeQuery(id+"F0.imprint","INTERSECT",VERTEX,{"disambiguationData":[OD(0.0)],"derivedFrom":[subQ1,subQ0]});Q62=makeQuery(id+"F0.imprint","IMPRINT",FACE,{"disambiguationData":[TD([[makeQuery(id+"F0.imprint","IMPRINT",EDGE,{"disambiguationData":[TD([[subQ2,-1.0]])],"derivedFrom":subQ1}),1.0]])]});}
            var Q63;
            {var subQ0=sQuery(id+"F0.wireOp",EDGE,"E281");var subQ1=sQuery(id+"F0.wireOp",EDGE,"E280");var subQ2=makeQuery(id+"F0.imprint","INTERSECT",VERTEX,{"disambiguationData":[OD(1.0)],"derivedFrom":[subQ1,subQ0]});Q63=makeQuery(id+"F0.imprint","IMPRINT",FACE,{"disambiguationData":[TD([[makeQuery(id+"F0.imprint","IMPRINT",EDGE,{"disambiguationData":[TD([[subQ2,1.0]])],"derivedFrom":subQ1}),1.0]])]});}
            var Q64;
            {var subQ0=sQuery(id+"F0.wireOp",EDGE,"E282");var subQ1=sQuery(id+"F0.wireOp",EDGE,"E280");var subQ2=makeQuery(id+"F0.imprint","INTERSECT",VERTEX,{"derivedFrom":[subQ1,subQ0]});Q64=makeQuery(id+"F0.imprint","IMPRINT",FACE,{"disambiguationData":[TD([[makeQuery(id+"F0.imprint","IMPRINT",EDGE,{"disambiguationData":[TD([[subQ2,-1.0]])],"derivedFrom":subQ1}),1.0]])]});}
            var Q65;
            {var subQ0=sQuery(id+"F0.wireOp",EDGE,"E283");var subQ1=sQuery(id+"F0.wireOp",EDGE,"E280");var subQ2=makeQuery(id+"F0.imprint","INTERSECT",VERTEX,{"disambiguationData":[OD(0.0)],"derivedFrom":[subQ1,subQ0]});Q65=makeQuery(id+"F0.imprint","IMPRINT",FACE,{"disambiguationData":[TD([[makeQuery(id+"F0.imprint","IMPRINT",EDGE,{"disambiguationData":[TD([[subQ2,-1.0]])],"derivedFrom":subQ1}),1.0]])]});}
            var Q66;
            {var subQ0=sQuery(id+"F0.wireOp",EDGE,"E283");var subQ1=sQuery(id+"F0.wireOp",EDGE,"E280");var subQ2=makeQuery(id+"F0.imprint","INTERSECT",VERTEX,{"disambiguationData":[OD(0.0)],"derivedFrom":[subQ1,subQ0]});Q66=makeQuery(id+"F0.imprint","IMPRINT",FACE,{"disambiguationData":[TD([[makeQuery(id+"F0.imprint","IMPRINT",EDGE,{"disambiguationData":[TD([[subQ2,-1.0]])],"derivedFrom":subQ1}),-1.0]])]});}
            var Q67;
            {var subQ0=sQuery(id+"F0.wireOp",EDGE,"E281");var subQ1=sQuery(id+"F0.wireOp",EDGE,"E280");var subQ2=makeQuery(id+"F0.imprint","INTERSECT",VERTEX,{"disambiguationData":[OD(0.0)],"derivedFrom":[subQ1,subQ0]});Q67=makeQuery(id+"F0.imprint","IMPRINT",FACE,{"disambiguationData":[TD([[makeQuery(id+"F0.imprint","IMPRINT",EDGE,{"disambiguationData":[TD([[subQ2,-1.0]])],"derivedFrom":subQ1}),-1.0]])]});}
            var Q68;
            {var subQ0=sQuery(id+"F0.wireOp",EDGE,"E281");var subQ1=sQuery(id+"F0.wireOp",EDGE,"E280");var subQ2=makeQuery(id+"F0.imprint","INTERSECT",VERTEX,{"disambiguationData":[OD(1.0)],"derivedFrom":[subQ1,subQ0]});Q68=makeQuery(id+"F0.imprint","IMPRINT",FACE,{"disambiguationData":[TD([[makeQuery(id+"F0.imprint","IMPRINT",EDGE,{"disambiguationData":[TD([[subQ2,1.0]])],"derivedFrom":subQ1}),-1.0]])]});}
            var Q69;
            {var subQ0=sQuery(id+"F0.wireOp",EDGE,"E282");var subQ1=sQuery(id+"F0.wireOp",EDGE,"E280");var subQ2=makeQuery(id+"F0.imprint","INTERSECT",VERTEX,{"derivedFrom":[subQ1,subQ0]});Q69=makeQuery(id+"F0.imprint","IMPRINT",FACE,{"disambiguationData":[TD([[makeQuery(id+"F0.imprint","IMPRINT",EDGE,{"disambiguationData":[TD([[subQ2,-1.0]])],"derivedFrom":subQ1}),-1.0]])]});}
            extrude(context, id + "F3", {"entities" : qUnion([Q0, Q1, Q2, Q3, Q4, Q5, Q6, Q7, Q8, Q9, Q10, Q11, Q12, Q13, Q14, Q15, Q16, Q17, Q18, Q19, Q20, Q21, Q22, Q23, Q24, Q25, Q26, Q27, Q28, Q29, Q30, Q31, Q32, Q33, Q34, Q35, Q36, Q37, Q38, Q39, Q40, Q41, Q42, Q43, Q44, Q45, Q46, Q47, Q48, Q49, Q50, Q51, Q52, Q53, Q54, Q55, Q56, Q57, Q58, Q59, Q60, Q61, Q62, Q63, Q64, Q65, Q66, Q67, Q68, Q69]), "depth" : 2.3 * mm});
        }
        {
            var Q0;
            {var subQ0=sQuery(id+"F0.wireOp",EDGE,"E356");var subQ1=sQuery(id+"F0.wireOp",EDGE,"E243");var subQ2=makeQuery(id+"F0.imprint","INTERSECT",VERTEX,{"disambiguationData":[OD(0.0)],"derivedFrom":[subQ1,subQ0]});Q0=makeQuery(id+"F0.imprint","IMPRINT",FACE,{"disambiguationData":[TD([[makeQuery(id+"F0.imprint","IMPRINT",EDGE,{"disambiguationData":[TD([[subQ2,1.0]])],"derivedFrom":subQ1}),-1.0]])]});}
            var Q1;
            {var subQ0=sQuery(id+"F0.wireOp",EDGE,"E355");var subQ1=sQuery(id+"F0.wireOp",EDGE,"E243");var subQ2=makeQuery(id+"F0.imprint","INTERSECT",VERTEX,{"disambiguationData":[OD(0.0)],"derivedFrom":[subQ1,subQ0]});Q1=makeQuery(id+"F0.imprint","IMPRINT",FACE,{"disambiguationData":[TD([[makeQuery(id+"F0.imprint","IMPRINT",EDGE,{"disambiguationData":[TD([[subQ2,1.0]])],"derivedFrom":subQ1}),-1.0]])]});}
            var Q2;
            {var subQ0=sQuery(id+"F0.wireOp",EDGE,"E355");var subQ1=sQuery(id+"F0.wireOp",EDGE,"E243");var subQ2=makeQuery(id+"F0.imprint","INTERSECT",VERTEX,{"disambiguationData":[OD(1.0)],"derivedFrom":[subQ1,subQ0]});Q2=makeQuery(id+"F0.imprint","IMPRINT",FACE,{"disambiguationData":[TD([[makeQuery(id+"F0.imprint","IMPRINT",EDGE,{"disambiguationData":[TD([[subQ2,-1.0]])],"derivedFrom":subQ1}),-1.0]])]});}
            var Q3;
            {var subQ0=sQuery(id+"F0.wireOp",EDGE,"E356");var subQ1=sQuery(id+"F0.wireOp",EDGE,"E243");var subQ2=makeQuery(id+"F0.imprint","INTERSECT",VERTEX,{"disambiguationData":[OD(0.0)],"derivedFrom":[subQ1,subQ0]});Q3=makeQuery(id+"F0.imprint","IMPRINT",FACE,{"disambiguationData":[TD([[makeQuery(id+"F0.imprint","IMPRINT",EDGE,{"disambiguationData":[TD([[subQ2,-1.0]])],"derivedFrom":subQ1}),-1.0]])]});}
            extrude(context, id + "F4", {"entities" : qUnion([Q0, Q1, Q2, Q3]), "oppositeDirection" : true, "depth" : 30 * mm});
        }
        {
            var Q0;
            Q0=makeQuery(id+"F0.imprint","IMPRINT",FACE,{"disambiguationData":[TD([[makeQuery(id+"F0.imprint","IMPRINT",EDGE,{"derivedFrom":sQuery(id+"F0.wireOp",EDGE,"E439.MirrorCS")}),1.0]])]});
            var Q1;
            Q1=makeQuery(id+"F0.imprint","IMPRINT",FACE,{"disambiguationData":[TD([[makeQuery(id+"F0.imprint","IMPRINT",EDGE,{"derivedFrom":sQuery(id+"F0.wireOp",EDGE,"E453.MirrorCS")}),-1.0]])]});
            var Q2;
            Q2=makeQuery(id+"F0.imprint","IMPRINT",FACE,{"disambiguationData":[TD([[makeQuery(id+"F0.imprint","IMPRINT",EDGE,{"derivedFrom":sQuery(id+"F0.wireOp",EDGE,"E448.MirrorCS")}),1.0]])]});
            var Q3;
            Q3=makeQuery(id+"F0.imprint","IMPRINT",FACE,{"disambiguationData":[TD([[makeQuery(id+"F0.imprint","IMPRINT",EDGE,{"derivedFrom":sQuery(id+"F0.wireOp",EDGE,"E446.MirrorCS")}),1.0]])]});
            extrude(context, id + "F5", {"entities" : qUnion([Q0, Q1, Q2, Q3]), "oppositeDirection" : true, "depth" : 9 * mm});
        }
    });
